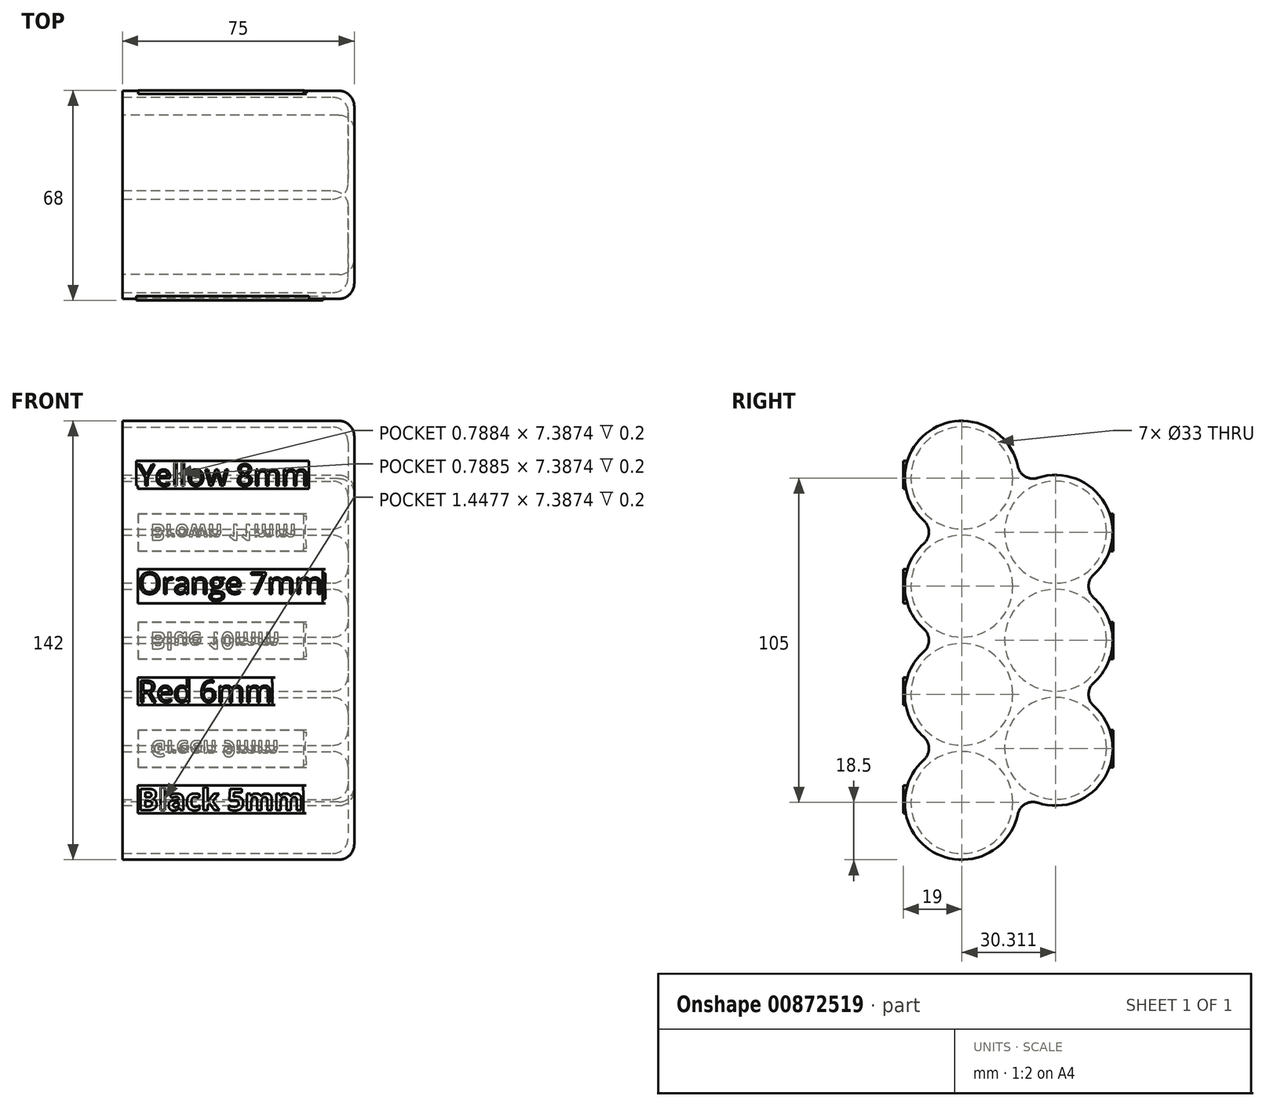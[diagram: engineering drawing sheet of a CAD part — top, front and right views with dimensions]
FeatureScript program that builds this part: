
annotation { "Feature Type Name" : "Feature", "Feature Type Description" : "" }
export const myFeature = defineFeature(function(context is Context, id is Id, definition is map)
    precondition{}
    {
        {
            var Q0;
            Q0=qCreatedBy(makeId("Top.planeOp"),FACE);
            var sketch = newSketch(context, id + "F0", { "sketchPlane" : qUnion([Q0])});
            skCircle(sketch, "E0", {"center": v(0, 0) * mm, "radius": 16.5 * mm});
            skCircle(sketch, "E1.1.0.0", {"center": v(35, 0) * mm, "radius": 16.5 * mm});
            skCircle(sketch, "E1.2.0.0", {"center": v(70, 0) * mm, "radius": 16.5 * mm});
            skCircle(sketch, "E1.3.0.0", {"center": v(105, 0) * mm, "radius": 16.5 * mm});
            skLineSegment(sketch, "E1.direction1", {"start": v(0, 0) * mm, "end": v(35, 0) * mm, "construction": true});
            skCircle(sketch, "E2", {"center": v(17.5, 30.31) * mm, "radius": 16.5 * mm});
            skCircle(sketch, "E3.1.0.0", {"center": v(52.5, 30.31) * mm, "radius": 16.5 * mm});
            skCircle(sketch, "E3.2.0.0", {"center": v(87.5, 30.31) * mm, "radius": 16.5 * mm});
            skLineSegment(sketch, "E3.direction1", {"start": v(17.5, 30.31) * mm, "end": v(52.5, 30.31) * mm, "construction": true});
            skCircle(sketch, "E4", {"center": v(0, 0) * mm, "radius": 18.5 * mm});
            skCircle(sketch, "E5.1.0.0", {"center": v(35, 0) * mm, "radius": 18.5 * mm});
            skCircle(sketch, "E5.2.0.0", {"center": v(70, 0) * mm, "radius": 18.5 * mm});
            skCircle(sketch, "E5.3.0.0", {"center": v(105, 0) * mm, "radius": 18.5 * mm});
            skCircle(sketch, "E6", {"center": v(17.5, 30.31) * mm, "radius": 18.5 * mm});
            skCircle(sketch, "E7.1.0.0", {"center": v(52.5, 30.31) * mm, "radius": 18.5 * mm});
            skCircle(sketch, "E7.2.0.0", {"center": v(87.5, 30.31) * mm, "radius": 18.5 * mm});
            skSolve(sketch);
        }
        {
            var Q0;
            {var subQ0=sQuery(id+"F0.wireOp",EDGE,"E7.1.0.0");var subQ1=sQuery(id+"F0.wireOp",EDGE,"E1.2.0.0");var subQ2=makeQuery(id+"F0.imprint","INTERSECT",VERTEX,{"derivedFrom":[subQ1,subQ0]});Q0=makeQuery(id+"F0.imprint","IMPRINT",FACE,{"disambiguationData":[TD([[makeQuery(id+"F0.imprint","IMPRINT",EDGE,{"disambiguationData":[TD([[subQ2,-1.0]])],"derivedFrom":subQ1}),-1.0]])]});}
            var Q1;
            {var subQ0=sQuery(id+"F0.wireOp",EDGE,"E5.1.0.0");var subQ1=sQuery(id+"F0.wireOp",EDGE,"E0");var subQ2=makeQuery(id+"F0.imprint","INTERSECT",VERTEX,{"derivedFrom":[subQ1,subQ0]});Q1=makeQuery(id+"F0.imprint","IMPRINT",FACE,{"disambiguationData":[TD([[makeQuery(id+"F0.imprint","IMPRINT",EDGE,{"disambiguationData":[TD([[subQ2,-1.0]])],"derivedFrom":subQ1}),-1.0]])]});}
            var Q2;
            {var subQ0=sQuery(id+"F0.wireOp",EDGE,"E7.2.0.0");var subQ1=sQuery(id+"F0.wireOp",EDGE,"E7.1.0.0");var subQ2=makeQuery(id+"F0.imprint","INTERSECT",VERTEX,{"disambiguationData":[OD(0.0)],"derivedFrom":[subQ1,subQ0]});Q2=makeQuery(id+"F0.imprint","IMPRINT",FACE,{"disambiguationData":[TD([[makeQuery(id+"F0.imprint","IMPRINT",EDGE,{"disambiguationData":[TD([[subQ2,1.0]])],"derivedFrom":subQ1}),1.0]])]});}
            var Q3;
            {var subQ0=sQuery(id+"F0.wireOp",EDGE,"E7.2.0.0");var subQ1=sQuery(id+"F0.wireOp",EDGE,"E1.2.0.0");var subQ2=makeQuery(id+"F0.imprint","INTERSECT",VERTEX,{"derivedFrom":[subQ1,subQ0]});Q3=makeQuery(id+"F0.imprint","IMPRINT",FACE,{"disambiguationData":[TD([[makeQuery(id+"F0.imprint","IMPRINT",EDGE,{"disambiguationData":[TD([[subQ2,1.0]])],"derivedFrom":subQ1}),-1.0]])]});}
            var Q4;
            {var subQ0=sQuery(id+"F0.wireOp",EDGE,"E7.2.0.0");var subQ1=sQuery(id+"F0.wireOp",EDGE,"E3.1.0.0");var subQ2=makeQuery(id+"F0.imprint","INTERSECT",VERTEX,{"derivedFrom":[subQ1,subQ0]});Q4=makeQuery(id+"F0.imprint","IMPRINT",FACE,{"disambiguationData":[TD([[makeQuery(id+"F0.imprint","IMPRINT",EDGE,{"disambiguationData":[TD([[subQ2,1.0]])],"derivedFrom":subQ1}),-1.0]])]});}
            var Q5;
            {var subQ0=sQuery(id+"F0.wireOp",EDGE,"E7.1.0.0");var subQ1=sQuery(id+"F0.wireOp",EDGE,"E3.2.0.0");var subQ2=makeQuery(id+"F0.imprint","INTERSECT",VERTEX,{"derivedFrom":[subQ1,subQ0]});Q5=makeQuery(id+"F0.imprint","IMPRINT",FACE,{"disambiguationData":[TD([[makeQuery(id+"F0.imprint","IMPRINT",EDGE,{"disambiguationData":[TD([[subQ2,1.0]])],"derivedFrom":subQ1}),-1.0]])]});}
            var Q6;
            {var subQ0=sQuery(id+"F0.wireOp",EDGE,"E5.2.0.0");var subQ1=sQuery(id+"F0.wireOp",EDGE,"E1.3.0.0");var subQ2=makeQuery(id+"F0.imprint","INTERSECT",VERTEX,{"derivedFrom":[subQ1,subQ0]});Q6=makeQuery(id+"F0.imprint","IMPRINT",FACE,{"disambiguationData":[TD([[makeQuery(id+"F0.imprint","IMPRINT",EDGE,{"disambiguationData":[TD([[subQ2,-1.0]])],"derivedFrom":subQ1}),-1.0]])]});}
            var Q7;
            {var subQ0=sQuery(id+"F0.wireOp",EDGE,"E5.2.0.0");var subQ1=sQuery(id+"F0.wireOp",EDGE,"E1.3.0.0");var subQ2=makeQuery(id+"F0.imprint","INTERSECT",VERTEX,{"derivedFrom":[subQ1,subQ0]});Q7=makeQuery(id+"F0.imprint","IMPRINT",FACE,{"disambiguationData":[TD([[makeQuery(id+"F0.imprint","IMPRINT",EDGE,{"disambiguationData":[TD([[subQ2,1.0]])],"derivedFrom":subQ1}),-1.0]])]});}
            var Q8;
            {var subQ0=sQuery(id+"F0.wireOp",EDGE,"E5.1.0.0");var subQ1=makeQuery(id+"F0.imprint","INTERSECT",VERTEX,{"derivedFrom":[sQuery(id+"F0.wireOp",EDGE,"E1.2.0.0"),subQ0]});Q8=makeQuery(id+"F0.imprint","IMPRINT",FACE,{"disambiguationData":[TD([[makeQuery(id+"F0.imprint","IMPRINT",EDGE,{"disambiguationData":[TD([[subQ1,-1.0]])],"derivedFrom":subQ0}),1.0]])]});}
            var Q9;
            {var subQ0=sQuery(id+"F0.wireOp",EDGE,"E5.1.0.0");var subQ1=sQuery(id+"F0.wireOp",EDGE,"E4");var subQ2=makeQuery(id+"F0.imprint","INTERSECT",VERTEX,{"disambiguationData":[OD(1.0)],"derivedFrom":[subQ1,subQ0]});Q9=makeQuery(id+"F0.imprint","IMPRINT",FACE,{"disambiguationData":[TD([[makeQuery(id+"F0.imprint","IMPRINT",EDGE,{"disambiguationData":[TD([[subQ2,-1.0]])],"derivedFrom":subQ1}),-1.0]])]});}
            var Q10;
            {var subQ0=sQuery(id+"F0.wireOp",EDGE,"E6");var subQ1=sQuery(id+"F0.wireOp",EDGE,"E1.1.0.0");var subQ2=makeQuery(id+"F0.imprint","INTERSECT",VERTEX,{"derivedFrom":[subQ1,subQ0]});Q10=makeQuery(id+"F0.imprint","IMPRINT",FACE,{"disambiguationData":[TD([[makeQuery(id+"F0.imprint","IMPRINT",EDGE,{"disambiguationData":[TD([[subQ2,-1.0]])],"derivedFrom":subQ1}),-1.0]])]});}
            var Q11;
            {var subQ0=sQuery(id+"F0.wireOp",EDGE,"E4");var subQ1=makeQuery(id+"F0.imprint","INTERSECT",VERTEX,{"derivedFrom":[sQuery(id+"F0.wireOp",EDGE,"E2"),subQ0]});Q11=makeQuery(id+"F0.imprint","IMPRINT",FACE,{"disambiguationData":[TD([[makeQuery(id+"F0.imprint","IMPRINT",EDGE,{"disambiguationData":[TD([[subQ1,1.0]])],"derivedFrom":subQ0}),1.0]])]});}
            var Q12;
            {var subQ0=sQuery(id+"F0.wireOp",EDGE,"E5.3.0.0");var subQ1=sQuery(id+"F0.wireOp",EDGE,"E5.2.0.0");var subQ2=makeQuery(id+"F0.imprint","INTERSECT",VERTEX,{"disambiguationData":[OD(1.0)],"derivedFrom":[subQ1,subQ0]});Q12=makeQuery(id+"F0.imprint","IMPRINT",FACE,{"disambiguationData":[TD([[makeQuery(id+"F0.imprint","IMPRINT",EDGE,{"disambiguationData":[TD([[subQ2,-1.0]])],"derivedFrom":subQ1}),-1.0]])]});}
            var Q13;
            {var subQ0=sQuery(id+"F0.wireOp",EDGE,"E5.2.0.0");var subQ1=sQuery(id+"F0.wireOp",EDGE,"E3.2.0.0");var subQ2=makeQuery(id+"F0.imprint","INTERSECT",VERTEX,{"derivedFrom":[subQ1,subQ0]});Q13=makeQuery(id+"F0.imprint","IMPRINT",FACE,{"disambiguationData":[TD([[makeQuery(id+"F0.imprint","IMPRINT",EDGE,{"disambiguationData":[TD([[subQ2,-1.0]])],"derivedFrom":subQ1}),-1.0]])]});}
            var Q14;
            {var subQ0=sQuery(id+"F0.wireOp",EDGE,"E5.1.0.0");var subQ1=sQuery(id+"F0.wireOp",EDGE,"E3.1.0.0");var subQ2=makeQuery(id+"F0.imprint","INTERSECT",VERTEX,{"derivedFrom":[subQ1,subQ0]});Q14=makeQuery(id+"F0.imprint","IMPRINT",FACE,{"disambiguationData":[TD([[makeQuery(id+"F0.imprint","IMPRINT",EDGE,{"disambiguationData":[TD([[subQ2,-1.0]])],"derivedFrom":subQ1}),-1.0]])]});}
            var Q15;
            {var subQ0=sQuery(id+"F0.wireOp",EDGE,"E5.1.0.0");var subQ1=makeQuery(id+"F0.imprint","INTERSECT",VERTEX,{"derivedFrom":[sQuery(id+"F0.wireOp",EDGE,"E3.1.0.0"),subQ0]});Q15=makeQuery(id+"F0.imprint","IMPRINT",FACE,{"disambiguationData":[TD([[makeQuery(id+"F0.imprint","IMPRINT",EDGE,{"disambiguationData":[TD([[subQ1,1.0]])],"derivedFrom":subQ0}),1.0]])]});}
            var Q16;
            {var subQ0=sQuery(id+"F0.wireOp",EDGE,"E6");var subQ1=sQuery(id+"F0.wireOp",EDGE,"E3.1.0.0");var subQ2=makeQuery(id+"F0.imprint","INTERSECT",VERTEX,{"derivedFrom":[subQ1,subQ0]});Q16=makeQuery(id+"F0.imprint","IMPRINT",FACE,{"disambiguationData":[TD([[makeQuery(id+"F0.imprint","IMPRINT",EDGE,{"disambiguationData":[TD([[subQ2,1.0]])],"derivedFrom":subQ1}),-1.0]])]});}
            var Q17;
            {var subQ0=sQuery(id+"F0.wireOp",EDGE,"E5.2.0.0");var subQ1=sQuery(id+"F0.wireOp",EDGE,"E1.1.0.0");var subQ2=makeQuery(id+"F0.imprint","INTERSECT",VERTEX,{"derivedFrom":[subQ1,subQ0]});Q17=makeQuery(id+"F0.imprint","IMPRINT",FACE,{"disambiguationData":[TD([[makeQuery(id+"F0.imprint","IMPRINT",EDGE,{"disambiguationData":[TD([[subQ2,1.0]])],"derivedFrom":subQ1}),-1.0]])]});}
            var Q18;
            {var subQ0=sQuery(id+"F0.wireOp",EDGE,"E4");var subQ1=sQuery(id+"F0.wireOp",EDGE,"E2");var subQ2=makeQuery(id+"F0.imprint","INTERSECT",VERTEX,{"derivedFrom":[subQ1,subQ0]});Q18=makeQuery(id+"F0.imprint","IMPRINT",FACE,{"disambiguationData":[TD([[makeQuery(id+"F0.imprint","IMPRINT",EDGE,{"disambiguationData":[TD([[subQ2,-1.0]])],"derivedFrom":subQ1}),-1.0]])]});}
            var Q19;
            {var subQ0=sQuery(id+"F0.wireOp",EDGE,"E5.2.0.0");var subQ1=sQuery(id+"F0.wireOp",EDGE,"E5.1.0.0");var subQ2=makeQuery(id+"F0.imprint","INTERSECT",VERTEX,{"disambiguationData":[OD(1.0)],"derivedFrom":[subQ1,subQ0]});Q19=makeQuery(id+"F0.imprint","IMPRINT",FACE,{"disambiguationData":[TD([[makeQuery(id+"F0.imprint","IMPRINT",EDGE,{"disambiguationData":[TD([[subQ2,-1.0]])],"derivedFrom":subQ1}),-1.0]])]});}
            var Q20;
            {var subQ0=sQuery(id+"F0.wireOp",EDGE,"E7.2.0.0");var subQ1=sQuery(id+"F0.wireOp",EDGE,"E1.2.0.0");var subQ2=makeQuery(id+"F0.imprint","INTERSECT",VERTEX,{"derivedFrom":[subQ1,subQ0]});Q20=makeQuery(id+"F0.imprint","IMPRINT",FACE,{"disambiguationData":[TD([[makeQuery(id+"F0.imprint","IMPRINT",EDGE,{"disambiguationData":[TD([[subQ2,-1.0]])],"derivedFrom":subQ1}),-1.0]])]});}
            var Q21;
            {var subQ0=sQuery(id+"F0.wireOp",EDGE,"E7.1.0.0");var subQ1=sQuery(id+"F0.wireOp",EDGE,"E2");var subQ2=makeQuery(id+"F0.imprint","INTERSECT",VERTEX,{"derivedFrom":[subQ1,subQ0]});Q21=makeQuery(id+"F0.imprint","IMPRINT",FACE,{"disambiguationData":[TD([[makeQuery(id+"F0.imprint","IMPRINT",EDGE,{"disambiguationData":[TD([[subQ2,1.0]])],"derivedFrom":subQ1}),-1.0]])]});}
            var Q22;
            {var subQ0=sQuery(id+"F0.wireOp",EDGE,"E5.1.0.0");var subQ1=makeQuery(id+"F0.imprint","INTERSECT",VERTEX,{"derivedFrom":[sQuery(id+"F0.wireOp",EDGE,"E2"),subQ0]});Q22=makeQuery(id+"F0.imprint","IMPRINT",FACE,{"disambiguationData":[TD([[makeQuery(id+"F0.imprint","IMPRINT",EDGE,{"disambiguationData":[TD([[subQ1,1.0]])],"derivedFrom":subQ0}),1.0]])]});}
            var Q23;
            {var subQ0=sQuery(id+"F0.wireOp",EDGE,"E6");var subQ1=sQuery(id+"F0.wireOp",EDGE,"E3.1.0.0");var subQ2=makeQuery(id+"F0.imprint","INTERSECT",VERTEX,{"derivedFrom":[subQ1,subQ0]});Q23=makeQuery(id+"F0.imprint","IMPRINT",FACE,{"disambiguationData":[TD([[makeQuery(id+"F0.imprint","IMPRINT",EDGE,{"disambiguationData":[TD([[subQ2,-1.0]])],"derivedFrom":subQ1}),-1.0]])]});}
            var Q24;
            {var subQ0=sQuery(id+"F0.wireOp",EDGE,"E4");var subQ1=makeQuery(id+"F0.imprint","INTERSECT",VERTEX,{"derivedFrom":[sQuery(id+"F0.wireOp",EDGE,"E1.1.0.0"),subQ0]});Q24=makeQuery(id+"F0.imprint","IMPRINT",FACE,{"disambiguationData":[TD([[makeQuery(id+"F0.imprint","IMPRINT",EDGE,{"disambiguationData":[TD([[subQ1,-1.0]])],"derivedFrom":subQ0}),1.0]])]});}
            var Q25;
            {var subQ0=sQuery(id+"F0.wireOp",EDGE,"E4");var subQ1=sQuery(id+"F0.wireOp",EDGE,"E2");var subQ2=makeQuery(id+"F0.imprint","INTERSECT",VERTEX,{"derivedFrom":[subQ1,subQ0]});Q25=makeQuery(id+"F0.imprint","IMPRINT",FACE,{"disambiguationData":[TD([[makeQuery(id+"F0.imprint","IMPRINT",EDGE,{"disambiguationData":[TD([[subQ2,1.0]])],"derivedFrom":subQ1}),-1.0]])]});}
            var Q26;
            {var subQ0=sQuery(id+"F0.wireOp",EDGE,"E5.2.0.0");var subQ1=makeQuery(id+"F0.imprint","INTERSECT",VERTEX,{"derivedFrom":[sQuery(id+"F0.wireOp",EDGE,"E3.2.0.0"),subQ0]});Q26=makeQuery(id+"F0.imprint","IMPRINT",FACE,{"disambiguationData":[TD([[makeQuery(id+"F0.imprint","IMPRINT",EDGE,{"disambiguationData":[TD([[subQ1,1.0]])],"derivedFrom":subQ0}),1.0]])]});}
            var Q27;
            {var subQ0=sQuery(id+"F0.wireOp",EDGE,"E7.1.0.0");var subQ1=sQuery(id+"F0.wireOp",EDGE,"E5.1.0.0");var subQ2=makeQuery(id+"F0.imprint","INTERSECT",VERTEX,{"disambiguationData":[OD(1.0)],"derivedFrom":[subQ1,subQ0]});Q27=makeQuery(id+"F0.imprint","IMPRINT",FACE,{"disambiguationData":[TD([[makeQuery(id+"F0.imprint","IMPRINT",EDGE,{"disambiguationData":[TD([[subQ2,-1.0]])],"derivedFrom":subQ1}),-1.0]])]});}
            var Q28;
            {var subQ0=sQuery(id+"F0.wireOp",EDGE,"E5.2.0.0");var subQ1=sQuery(id+"F0.wireOp",EDGE,"E3.2.0.0");var subQ2=makeQuery(id+"F0.imprint","INTERSECT",VERTEX,{"derivedFrom":[subQ1,subQ0]});Q28=makeQuery(id+"F0.imprint","IMPRINT",FACE,{"disambiguationData":[TD([[makeQuery(id+"F0.imprint","IMPRINT",EDGE,{"disambiguationData":[TD([[subQ2,1.0]])],"derivedFrom":subQ1}),-1.0]])]});}
            var Q29;
            {var subQ0=sQuery(id+"F0.wireOp",EDGE,"E5.3.0.0");var subQ1=sQuery(id+"F0.wireOp",EDGE,"E1.2.0.0");var subQ2=makeQuery(id+"F0.imprint","INTERSECT",VERTEX,{"derivedFrom":[subQ1,subQ0]});Q29=makeQuery(id+"F0.imprint","IMPRINT",FACE,{"disambiguationData":[TD([[makeQuery(id+"F0.imprint","IMPRINT",EDGE,{"disambiguationData":[TD([[subQ2,1.0]])],"derivedFrom":subQ1}),-1.0]])]});}
            var Q30;
            {var subQ0=sQuery(id+"F0.wireOp",EDGE,"E7.1.0.0");var subQ1=sQuery(id+"F0.wireOp",EDGE,"E1.1.0.0");var subQ2=makeQuery(id+"F0.imprint","INTERSECT",VERTEX,{"derivedFrom":[subQ1,subQ0]});Q30=makeQuery(id+"F0.imprint","IMPRINT",FACE,{"disambiguationData":[TD([[makeQuery(id+"F0.imprint","IMPRINT",EDGE,{"disambiguationData":[TD([[subQ2,-1.0]])],"derivedFrom":subQ1}),-1.0]])]});}
            var Q31;
            {var subQ0=sQuery(id+"F0.wireOp",EDGE,"E5.2.0.0");var subQ1=makeQuery(id+"F0.imprint","INTERSECT",VERTEX,{"derivedFrom":[sQuery(id+"F0.wireOp",EDGE,"E1.3.0.0"),subQ0]});Q31=makeQuery(id+"F0.imprint","IMPRINT",FACE,{"disambiguationData":[TD([[makeQuery(id+"F0.imprint","IMPRINT",EDGE,{"disambiguationData":[TD([[subQ1,-1.0]])],"derivedFrom":subQ0}),1.0]])]});}
            var Q32;
            {var subQ0=sQuery(id+"F0.wireOp",EDGE,"E7.2.0.0");var subQ1=sQuery(id+"F0.wireOp",EDGE,"E5.2.0.0");var subQ2=makeQuery(id+"F0.imprint","INTERSECT",VERTEX,{"disambiguationData":[OD(1.0)],"derivedFrom":[subQ1,subQ0]});Q32=makeQuery(id+"F0.imprint","IMPRINT",FACE,{"disambiguationData":[TD([[makeQuery(id+"F0.imprint","IMPRINT",EDGE,{"disambiguationData":[TD([[subQ2,-1.0]])],"derivedFrom":subQ1}),-1.0]])]});}
            var Q33;
            {var subQ0=sQuery(id+"F0.wireOp",EDGE,"E7.1.0.0");var subQ1=sQuery(id+"F0.wireOp",EDGE,"E1.1.0.0");var subQ2=makeQuery(id+"F0.imprint","INTERSECT",VERTEX,{"derivedFrom":[subQ1,subQ0]});Q33=makeQuery(id+"F0.imprint","IMPRINT",FACE,{"disambiguationData":[TD([[makeQuery(id+"F0.imprint","IMPRINT",EDGE,{"disambiguationData":[TD([[subQ2,1.0]])],"derivedFrom":subQ1}),-1.0]])]});}
            var Q34;
            {var subQ0=sQuery(id+"F0.wireOp",EDGE,"E5.2.0.0");var subQ1=makeQuery(id+"F0.imprint","INTERSECT",VERTEX,{"derivedFrom":[sQuery(id+"F0.wireOp",EDGE,"E3.1.0.0"),subQ0]});Q34=makeQuery(id+"F0.imprint","IMPRINT",FACE,{"disambiguationData":[TD([[makeQuery(id+"F0.imprint","IMPRINT",EDGE,{"disambiguationData":[TD([[subQ1,1.0]])],"derivedFrom":subQ0}),1.0]])]});}
            var Q35;
            {var subQ0=sQuery(id+"F0.wireOp",EDGE,"E7.2.0.0");var subQ1=sQuery(id+"F0.wireOp",EDGE,"E5.3.0.0");var subQ2=makeQuery(id+"F0.imprint","INTERSECT",VERTEX,{"disambiguationData":[OD(0.0)],"derivedFrom":[subQ1,subQ0]});Q35=makeQuery(id+"F0.imprint","IMPRINT",FACE,{"disambiguationData":[TD([[makeQuery(id+"F0.imprint","IMPRINT",EDGE,{"disambiguationData":[TD([[subQ2,-1.0]])],"derivedFrom":subQ1}),1.0]])]});}
            var Q36;
            {var subQ0=sQuery(id+"F0.wireOp",EDGE,"E5.1.0.0");var subQ1=sQuery(id+"F0.wireOp",EDGE,"E0");var subQ2=makeQuery(id+"F0.imprint","INTERSECT",VERTEX,{"derivedFrom":[subQ1,subQ0]});Q36=makeQuery(id+"F0.imprint","IMPRINT",FACE,{"disambiguationData":[TD([[makeQuery(id+"F0.imprint","IMPRINT",EDGE,{"disambiguationData":[TD([[subQ2,1.0]])],"derivedFrom":subQ1}),-1.0]])]});}
            var Q37;
            {var subQ0=sQuery(id+"F0.wireOp",EDGE,"E7.1.0.0");var subQ1=sQuery(id+"F0.wireOp",EDGE,"E6");var subQ2=makeQuery(id+"F0.imprint","INTERSECT",VERTEX,{"disambiguationData":[OD(0.0)],"derivedFrom":[subQ1,subQ0]});Q37=makeQuery(id+"F0.imprint","IMPRINT",FACE,{"disambiguationData":[TD([[makeQuery(id+"F0.imprint","IMPRINT",EDGE,{"disambiguationData":[TD([[subQ2,1.0]])],"derivedFrom":subQ1}),1.0]])]});}
            extrude(context, id + "F1", {"entities" : qUnion([Q0, Q1, Q2, Q3, Q4, Q5, Q6, Q7, Q8, Q9, Q10, Q11, Q12, Q13, Q14, Q15, Q16, Q17, Q18, Q19, Q20, Q21, Q22, Q23, Q24, Q25, Q26, Q27, Q28, Q29, Q30, Q31, Q32, Q33, Q34, Q35, Q36, Q37]), "depth" : 75 * mm, "offsetDistance" : 25 * mm});
        }
        {
            var Q0;
            {var subQ0=sQuery(id+"F0.wireOp",EDGE,"E0");var subQ1=makeQuery(id+"F0.imprint","INTERSECT",VERTEX,{"derivedFrom":[subQ0,sQuery(id+"F0.wireOp",EDGE,"E5.1.0.0")]});Q0=makeQuery(id+"F0.imprint","IMPRINT",FACE,{"disambiguationData":[TD([[makeQuery(id+"F0.imprint","IMPRINT",EDGE,{"disambiguationData":[TD([[subQ1,-1.0]])],"derivedFrom":subQ0}),1.0]])]});}
            var Q1;
            {var subQ0=sQuery(id+"F0.wireOp",EDGE,"E2");var subQ1=makeQuery(id+"F0.imprint","INTERSECT",VERTEX,{"derivedFrom":[subQ0,sQuery(id+"F0.wireOp",EDGE,"E4")]});Q1=makeQuery(id+"F0.imprint","IMPRINT",FACE,{"disambiguationData":[TD([[makeQuery(id+"F0.imprint","IMPRINT",EDGE,{"disambiguationData":[TD([[subQ1,1.0]])],"derivedFrom":subQ0}),1.0]])]});}
            var Q2;
            {var subQ0=sQuery(id+"F0.wireOp",EDGE,"E3.1.0.0");var subQ1=makeQuery(id+"F0.imprint","INTERSECT",VERTEX,{"derivedFrom":[subQ0,sQuery(id+"F0.wireOp",EDGE,"E6")]});Q2=makeQuery(id+"F0.imprint","IMPRINT",FACE,{"disambiguationData":[TD([[makeQuery(id+"F0.imprint","IMPRINT",EDGE,{"disambiguationData":[TD([[subQ1,1.0]])],"derivedFrom":subQ0}),1.0]])]});}
            var Q3;
            {var subQ0=sQuery(id+"F0.wireOp",EDGE,"E3.2.0.0");var subQ1=makeQuery(id+"F0.imprint","INTERSECT",VERTEX,{"derivedFrom":[subQ0,sQuery(id+"F0.wireOp",EDGE,"E5.2.0.0")]});Q3=makeQuery(id+"F0.imprint","IMPRINT",FACE,{"disambiguationData":[TD([[makeQuery(id+"F0.imprint","IMPRINT",EDGE,{"disambiguationData":[TD([[subQ1,1.0]])],"derivedFrom":subQ0}),1.0]])]});}
            var Q4;
            {var subQ0=sQuery(id+"F0.wireOp",EDGE,"E1.3.0.0");var subQ1=makeQuery(id+"F0.imprint","INTERSECT",VERTEX,{"derivedFrom":[subQ0,sQuery(id+"F0.wireOp",EDGE,"E5.2.0.0")]});Q4=makeQuery(id+"F0.imprint","IMPRINT",FACE,{"disambiguationData":[TD([[makeQuery(id+"F0.imprint","IMPRINT",EDGE,{"disambiguationData":[TD([[subQ1,1.0]])],"derivedFrom":subQ0}),1.0]])]});}
            var Q5;
            {var subQ0=sQuery(id+"F0.wireOp",EDGE,"E1.2.0.0");var subQ1=makeQuery(id+"F0.imprint","INTERSECT",VERTEX,{"derivedFrom":[subQ0,sQuery(id+"F0.wireOp",EDGE,"E7.2.0.0")]});Q5=makeQuery(id+"F0.imprint","IMPRINT",FACE,{"disambiguationData":[TD([[makeQuery(id+"F0.imprint","IMPRINT",EDGE,{"disambiguationData":[TD([[subQ1,1.0]])],"derivedFrom":subQ0}),1.0]])]});}
            var Q6;
            {var subQ0=sQuery(id+"F0.wireOp",EDGE,"E1.1.0.0");var subQ1=makeQuery(id+"F0.imprint","INTERSECT",VERTEX,{"derivedFrom":[subQ0,sQuery(id+"F0.wireOp",EDGE,"E7.1.0.0")]});Q6=makeQuery(id+"F0.imprint","IMPRINT",FACE,{"disambiguationData":[TD([[makeQuery(id+"F0.imprint","IMPRINT",EDGE,{"disambiguationData":[TD([[subQ1,1.0]])],"derivedFrom":subQ0}),1.0]])]});}
            extrude(context, id + "F2", {"entities" : qUnion([Q0, Q1, Q2, Q3, Q4, Q5, Q6]), "operationType" : NewBodyOperationType.ADD, "depth" : 2 * mm, "offsetDistance" : 25 * mm});
        }
        {
            var Q0;
            Q0=makeQuery(id+"F1.opExtrude","SWEPT_EDGE",EDGE,{"disambiguationData":[OSD([sQuery(id+"F0.wireOp",EDGE,"E5.2.0.0"),sQuery(id+"F0.wireOp",EDGE,"E5.3.0.0")])]});
            var Q1;
            Q1=makeQuery(id+"F1.opExtrude","SWEPT_EDGE",EDGE,{"disambiguationData":[OSD([sQuery(id+"F0.wireOp",EDGE,"E5.1.0.0"),sQuery(id+"F0.wireOp",EDGE,"E5.2.0.0")])]});
            var Q2;
            Q2=makeQuery(id+"F1.opExtrude","SWEPT_EDGE",EDGE,{"disambiguationData":[OSD([sQuery(id+"F0.wireOp",EDGE,"E4"),sQuery(id+"F0.wireOp",EDGE,"E5.1.0.0")])]});
            var Q3;
            Q3=makeQuery(id+"F1.opExtrude","SWEPT_EDGE",EDGE,{"disambiguationData":[OSD([sQuery(id+"F0.wireOp",EDGE,"E7.1.0.0"),sQuery(id+"F0.wireOp",EDGE,"E7.2.0.0")])]});
            var Q4;
            Q4=makeQuery(id+"F1.opExtrude","SWEPT_EDGE",EDGE,{"disambiguationData":[OSD([sQuery(id+"F0.wireOp",EDGE,"E6"),sQuery(id+"F0.wireOp",EDGE,"E7.1.0.0")])]});
            var Q5;
            Q5=makeQuery(id+"F1.opExtrude","SWEPT_EDGE",EDGE,{"disambiguationData":[OSD([sQuery(id+"F0.wireOp",EDGE,"E4"),sQuery(id+"F0.wireOp",EDGE,"E6")])]});
            var Q6;
            Q6=makeQuery(id+"F1.opExtrude","SWEPT_EDGE",EDGE,{"disambiguationData":[OSD([sQuery(id+"F0.wireOp",EDGE,"E5.3.0.0"),sQuery(id+"F0.wireOp",EDGE,"E7.2.0.0")])]});
            fillet(context, id + "F3", {"entities" : qUnion([Q0, Q1, Q2, Q3, Q4, Q5, Q6]), "radius" : 5 * mm, "tangentPropagation" : true, "allowEdgeOverflow" : false});
        }
        {
            var Q0;
            {var subQ0=sQuery(id+"F0.wireOp",EDGE,"E3.2.0.0");var subQ1=sQuery(id+"F0.wireOp",EDGE,"E3.1.0.0");var subQ2=sQuery(id+"F0.wireOp",EDGE,"E2");var subQ3=sQuery(id+"F0.wireOp",EDGE,"E1.3.0.0");var subQ4=sQuery(id+"F0.wireOp",EDGE,"E1.2.0.0");var subQ5=sQuery(id+"F0.wireOp",EDGE,"E1.1.0.0");var subQ6=sQuery(id+"F0.wireOp",EDGE,"E0");Q0=makeQuery(id+"F2.boolean.opBoolean","MERGE",FACE,{"derivedFrom":[makeQuery(id+"F1.opExtrude","CAP_FACE",FACE,{"disambiguationData":[OSD([subQ6,subQ5,subQ4,subQ3,subQ2,subQ1,subQ0,sQuery(id+"F0.wireOp",EDGE,"E4"),sQuery(id+"F0.wireOp",EDGE,"E5.1.0.0"),sQuery(id+"F0.wireOp",EDGE,"E5.2.0.0"),sQuery(id+"F0.wireOp",EDGE,"E5.3.0.0"),sQuery(id+"F0.wireOp",EDGE,"E6"),sQuery(id+"F0.wireOp",EDGE,"E7.1.0.0"),sQuery(id+"F0.wireOp",EDGE,"E7.2.0.0")])],"isStart":true}),makeQuery(id+"F2.opExtrude","CAP_FACE",FACE,{"disambiguationData":[OSD([subQ6])],"isStart":true}),makeQuery(id+"F2.opExtrude","CAP_FACE",FACE,{"disambiguationData":[OSD([subQ5])],"isStart":true}),makeQuery(id+"F2.opExtrude","CAP_FACE",FACE,{"disambiguationData":[OSD([subQ4])],"isStart":true}),makeQuery(id+"F2.opExtrude","CAP_FACE",FACE,{"disambiguationData":[OSD([subQ3])],"isStart":true}),makeQuery(id+"F2.opExtrude","CAP_FACE",FACE,{"disambiguationData":[OSD([subQ2])],"isStart":true}),makeQuery(id+"F2.opExtrude","CAP_FACE",FACE,{"disambiguationData":[OSD([subQ1])],"isStart":true}),makeQuery(id+"F2.opExtrude","CAP_FACE",FACE,{"disambiguationData":[OSD([subQ0])],"isStart":true})]});}
            fillet(context, id + "F4", {"entities" : qUnion([Q0]), "radius" : 5 * mm, "tangentPropagation" : true, "allowEdgeOverflow" : false});
        }
        {
            var Q0;
            Q0=makeQuery(id+"F2.opExtrude","CAP_FACE",FACE,{"disambiguationData":[OSD([sQuery(id+"F0.wireOp",EDGE,"E2")])],"isStart":false});
            var Q1;
            Q1=makeQuery(id+"F2.opExtrude","CAP_FACE",FACE,{"disambiguationData":[OSD([sQuery(id+"F0.wireOp",EDGE,"E3.1.0.0")])],"isStart":false});
            var Q2;
            Q2=makeQuery(id+"F2.opExtrude","CAP_FACE",FACE,{"disambiguationData":[OSD([sQuery(id+"F0.wireOp",EDGE,"E3.2.0.0")])],"isStart":false});
            var Q3;
            Q3=makeQuery(id+"F2.opExtrude","CAP_FACE",FACE,{"disambiguationData":[OSD([sQuery(id+"F0.wireOp",EDGE,"E1.3.0.0")])],"isStart":false});
            var Q4;
            Q4=makeQuery(id+"F2.opExtrude","CAP_FACE",FACE,{"disambiguationData":[OSD([sQuery(id+"F0.wireOp",EDGE,"E1.2.0.0")])],"isStart":false});
            var Q5;
            Q5=makeQuery(id+"F2.opExtrude","CAP_FACE",FACE,{"disambiguationData":[OSD([sQuery(id+"F0.wireOp",EDGE,"E1.1.0.0")])],"isStart":false});
            var Q6;
            Q6=makeQuery(id+"F2.opExtrude","CAP_FACE",FACE,{"disambiguationData":[OSD([sQuery(id+"F0.wireOp",EDGE,"E0")])],"isStart":false});
            fillet(context, id + "F5", {"entities" : qUnion([Q0, Q1, Q2, Q3, Q4, Q5, Q6]), "radius" : 5 * mm, "tangentPropagation" : true, "allowEdgeOverflow" : false});
        }
        {
            var Q0;
            Q0=qCreatedBy(makeId("Front.planeOp"),FACE);
            cPlane(context, id + "F6", {"entities" : qUnion([Q0]), "cplaneType" : CPlaneType.OFFSET, "offset" : 19 * mm, "width" : 150 * mm, "height" : 150 * mm});
        }
        {
            var Q0;
            Q0=qCreatedBy(makeId("Right.planeOp"),FACE);
            var sketch = newSketch(context, id + "F7", { "sketchPlane" : qUnion([Q0])});
            skLineSegment(sketch, "E8", {"start": v(0, 0) * mm, "end": v(-52.63, 0) * mm, "construction": true});
            skSolve(sketch);
        }
        {
            var Q0;
            Q0=makeQuery(id+"F1.opExtrude","SWEPT_BODY",BODY,{"disambiguationData":[OSD([sQuery(id+"F0.wireOp",EDGE,"E0"),sQuery(id+"F0.wireOp",EDGE,"E1.1.0.0"),sQuery(id+"F0.wireOp",EDGE,"E1.2.0.0"),sQuery(id+"F0.wireOp",EDGE,"E1.3.0.0"),sQuery(id+"F0.wireOp",EDGE,"E2"),sQuery(id+"F0.wireOp",EDGE,"E3.1.0.0"),sQuery(id+"F0.wireOp",EDGE,"E3.2.0.0"),sQuery(id+"F0.wireOp",EDGE,"E4"),sQuery(id+"F0.wireOp",EDGE,"E5.1.0.0"),sQuery(id+"F0.wireOp",EDGE,"E5.2.0.0"),sQuery(id+"F0.wireOp",EDGE,"E5.3.0.0"),sQuery(id+"F0.wireOp",EDGE,"E6"),sQuery(id+"F0.wireOp",EDGE,"E7.1.0.0"),sQuery(id+"F0.wireOp",EDGE,"E7.2.0.0")])]});
            var Q1;
            Q1=sQuery(id+"F7.wireOp",EDGE,"E8");
            transform(context, id + "F8", {"entities" : qUnion([Q0]), "transformType" : TransformType.ROTATION, "transformAxis" : qUnion([Q1]), "angle" : 90 * degree, "makeCopy" : false});
        }
        {
            var Q0;
            Q0=qCreatedBy(id+"F6.planeOp",FACE);
            var sketch = newSketch(context, id + "F9", { "sketchPlane" : qUnion([Q0])});
            skLineSegment(sketch, "E9", {"start": v(-70, -17.5) * mm, "end": v(-70, 139.56) * mm, "construction": true});
            skText(sketch, "E10", { "text": "Black 5mm", "fontName": "OpenSans-Bold.ttf"});
            skText(sketch, "E11", { "text": "Red 6mm\n", "fontName": "OpenSans-Regular.ttf"});
            skText(sketch, "E12", { "text": "Orange 7mm\n", "fontName": "OpenSans-Regular.ttf"});
            skText(sketch, "E13", { "text": "Yellow 8mm\n", "fontName": "OpenSans-Regular.ttf"});
            skLineSegment(sketch, "E14.bottom", {"start": v(-70, 5.5) * mm, "end": v(-16.53, 5.5) * mm});
            skLineSegment(sketch, "E14.top", {"start": v(-70, -3.5) * mm, "end": v(-16.53, -3.5) * mm});
            skLineSegment(sketch, "E14.left", {"start": v(-70, 5.5) * mm, "end": v(-70, -3.5) * mm});
            skLineSegment(sketch, "E14.right", {"start": v(-16.53, 5.5) * mm, "end": v(-16.53, -3.5) * mm});
            skLineSegment(sketch, "E15.bottom", {"start": v(-70, 40.5) * mm, "end": v(-26.56, 40.5) * mm});
            skLineSegment(sketch, "E15.top", {"start": v(-70, 31.5) * mm, "end": v(-26.56, 31.5) * mm});
            skLineSegment(sketch, "E15.left", {"start": v(-70, 40.5) * mm, "end": v(-70, 31.5) * mm});
            skLineSegment(sketch, "E15.right", {"start": v(-26.56, 40.5) * mm, "end": v(-26.56, 31.5) * mm});
            skLineSegment(sketch, "E16.bottom", {"start": v(-70, 75.5) * mm, "end": v(-10.3, 75.5) * mm});
            skLineSegment(sketch, "E16.top", {"start": v(-70, 64.5) * mm, "end": v(-10.3, 64.5) * mm});
            skLineSegment(sketch, "E16.left", {"start": v(-70, 75.5) * mm, "end": v(-70, 64.5) * mm});
            skLineSegment(sketch, "E16.right", {"start": v(-10.3, 75.5) * mm, "end": v(-10.3, 64.5) * mm});
            skPoint(sketch, "E17.oppositeSnap0", {"position": v(-14.73, 106) * mm});
            skLineSegment(sketch, "E17.bottom", {"start": v(-70, 110.5) * mm, "end": v(-14.73, 110.5) * mm});
            skLineSegment(sketch, "E17.top", {"start": v(-70, 101.5) * mm, "end": v(-14.73, 101.5) * mm});
            skLineSegment(sketch, "E17.left", {"start": v(-70, 110.5) * mm, "end": v(-70, 101.5) * mm});
            skLineSegment(sketch, "E17.right", {"start": v(-14.73, 110.5) * mm, "end": v(-14.73, 101.5) * mm});
            skLineSegment(sketch, "E18.bottom", {"start": v(-70, 110.5) * mm, "end": v(-70.5, 110.5) * mm});
            skLineSegment(sketch, "E18.top", {"start": v(-70, 102.5) * mm, "end": v(-70.5, 102.5) * mm});
            skLineSegment(sketch, "E18.left", {"start": v(-70, 110.5) * mm, "end": v(-70, 102.5) * mm});
            skLineSegment(sketch, "E18.right", {"start": v(-70.5, 110.5) * mm, "end": v(-70.5, 102.5) * mm});
            skLineSegment(sketch, "E19.bottom", {"start": v(-70.5, 102.5) * mm, "end": v(-70, 102.5) * mm});
            skLineSegment(sketch, "E19.top", {"start": v(-70.5, 101.5) * mm, "end": v(-70, 101.5) * mm});
            skLineSegment(sketch, "E19.left", {"start": v(-70.5, 102.5) * mm, "end": v(-70.5, 101.5) * mm});
            skLineSegment(sketch, "E19.right", {"start": v(-70, 102.5) * mm, "end": v(-70, 101.5) * mm});
            const initialGuessF9  = {"E10": [-0.07, -0.0025, 1, 0, 0.007], "E11": [-0.07, 0.0325, 1, 0, 0.007], "E12": [-0.07, 0.0675, 1, 0, 0.007], "E13": [-0.07, 0.1025, 1, 0, 0.007]};
            skSetInitialGuess(sketch, initialGuessF9);
            skSolve(sketch);
        }
        {
            var Q0;
            Q0=makeQuery(id+"F9.imprint","IMPRINT",FACE,{"disambiguationData":[TD([[makeQuery(id+"F9.imprint","IMPRINT",EDGE,{"derivedFrom":sQuery(id+"F9.wireOp",EDGE,"E10.sketch_text.stroke-0")}),1.0]])]});
            var Q1;
            Q1=makeQuery(id+"F9.imprint","IMPRINT",FACE,{"disambiguationData":[TD([[makeQuery(id+"F9.imprint","IMPRINT",EDGE,{"derivedFrom":sQuery(id+"F9.wireOp",EDGE,"E10.sketch_text.stroke-47")}),1.0]])]});
            var Q2;
            Q2=makeQuery(id+"F9.imprint","IMPRINT",FACE,{"disambiguationData":[TD([[makeQuery(id+"F9.imprint","IMPRINT",EDGE,{"derivedFrom":sQuery(id+"F9.wireOp",EDGE,"E10.sketch_text.stroke-19")}),1.0]])]});
            var Q3;
            Q3=makeQuery(id+"F9.imprint","IMPRINT",FACE,{"disambiguationData":[TD([[makeQuery(id+"F9.imprint","IMPRINT",EDGE,{"derivedFrom":sQuery(id+"F9.wireOp",EDGE,"E10.sketch_text.stroke-12")}),1.0]])]});
            var Q4;
            Q4=makeQuery(id+"F9.imprint","IMPRINT",FACE,{"disambiguationData":[TD([[makeQuery(id+"F9.imprint","IMPRINT",EDGE,{"derivedFrom":sQuery(id+"F9.wireOp",EDGE,"E11.sketch_text.stroke-0")}),1.0]])]});
            var Q5;
            Q5=makeQuery(id+"F9.imprint","IMPRINT",FACE,{"disambiguationData":[TD([[makeQuery(id+"F9.imprint","IMPRINT",EDGE,{"derivedFrom":sQuery(id+"F9.wireOp",EDGE,"E11.sketch_text.stroke-76")}),1.0]])]});
            var Q6;
            Q6=makeQuery(id+"F9.imprint","IMPRINT",FACE,{"disambiguationData":[TD([[makeQuery(id+"F9.imprint","IMPRINT",EDGE,{"derivedFrom":sQuery(id+"F9.wireOp",EDGE,"E11.sketch_text.stroke-52")}),1.0]])]});
            var Q7;
            Q7=makeQuery(id+"F9.imprint","IMPRINT",FACE,{"disambiguationData":[TD([[makeQuery(id+"F9.imprint","IMPRINT",EDGE,{"derivedFrom":sQuery(id+"F9.wireOp",EDGE,"E11.sketch_text.stroke-11")}),1.0]])]});
            var Q8;
            Q8=makeQuery(id+"F9.imprint","IMPRINT",FACE,{"disambiguationData":[TD([[makeQuery(id+"F9.imprint","IMPRINT",EDGE,{"derivedFrom":sQuery(id+"F9.wireOp",EDGE,"E11.sketch_text.stroke-32")}),1.0]])]});
            var Q9;
            Q9=makeQuery(id+"F9.imprint","IMPRINT",FACE,{"disambiguationData":[TD([[makeQuery(id+"F9.imprint","IMPRINT",EDGE,{"derivedFrom":sQuery(id+"F9.wireOp",EDGE,"E12.sketch_text.stroke-0")}),1.0]])]});
            var Q10;
            Q10=makeQuery(id+"F9.imprint","IMPRINT",FACE,{"disambiguationData":[TD([[makeQuery(id+"F9.imprint","IMPRINT",EDGE,{"derivedFrom":sQuery(id+"F9.wireOp",EDGE,"E12.sketch_text.stroke-48")}),1.0]])]});
            var Q11;
            Q11=makeQuery(id+"F9.imprint","IMPRINT",FACE,{"disambiguationData":[TD([[makeQuery(id+"F9.imprint","IMPRINT",EDGE,{"derivedFrom":sQuery(id+"F9.wireOp",EDGE,"E12.sketch_text.stroke-8")}),1.0]])]});
            var Q12;
            Q12=makeQuery(id+"F9.imprint","IMPRINT",FACE,{"disambiguationData":[TD([[makeQuery(id+"F9.imprint","IMPRINT",EDGE,{"derivedFrom":sQuery(id+"F9.wireOp",EDGE,"E12.sketch_text.stroke-111")}),1.0]])]});
            var Q13;
            Q13=makeQuery(id+"F9.imprint","IMPRINT",FACE,{"disambiguationData":[TD([[makeQuery(id+"F9.imprint","IMPRINT",EDGE,{"derivedFrom":sQuery(id+"F9.wireOp",EDGE,"E12.sketch_text.stroke-102")}),1.0]])]});
            var Q14;
            Q14=makeQuery(id+"F9.imprint","IMPRINT",FACE,{"disambiguationData":[TD([[makeQuery(id+"F9.imprint","IMPRINT",EDGE,{"derivedFrom":sQuery(id+"F9.wireOp",EDGE,"E12.sketch_text.stroke-131")}),1.0]])]});
            var Q15;
            Q15=makeQuery(id+"F9.imprint","IMPRINT",FACE,{"disambiguationData":[TD([[makeQuery(id+"F9.imprint","IMPRINT",EDGE,{"derivedFrom":sQuery(id+"F9.wireOp",EDGE,"E13.sketch_text.stroke-0")}),1.0]])]});
            var Q16;
            {var subQ3=sQuery(id+"F9.wireOp",EDGE,"E18.bottom");Q16=makeQuery(id+"F9.imprint","IMPRINT",FACE,{"disambiguationData":[TD([[makeQuery(id+"F9.imprint","IMPRINT",EDGE,{"derivedFrom":subQ3}),1.0]])]});}
            var Q17;
            Q17=makeQuery(id+"F9.imprint","IMPRINT",FACE,{"disambiguationData":[TD([[makeQuery(id+"F9.imprint","IMPRINT",EDGE,{"derivedFrom":sQuery(id+"F9.wireOp",EDGE,"E19.bottom")}),-1.0]])]});
            var Q18;
            Q18=makeQuery(id+"F9.imprint","IMPRINT",FACE,{"disambiguationData":[TD([[makeQuery(id+"F9.imprint","IMPRINT",EDGE,{"derivedFrom":sQuery(id+"F9.wireOp",EDGE,"E13.sketch_text.stroke-23")}),1.0]])]});
            var Q19;
            Q19=makeQuery(id+"F9.imprint","IMPRINT",FACE,{"disambiguationData":[TD([[makeQuery(id+"F9.imprint","IMPRINT",EDGE,{"derivedFrom":sQuery(id+"F9.wireOp",EDGE,"E13.sketch_text.stroke-45")}),1.0]])]});
            var Q20;
            Q20=makeQuery(id+"F9.imprint","IMPRINT",FACE,{"disambiguationData":[TD([[makeQuery(id+"F9.imprint","IMPRINT",EDGE,{"derivedFrom":sQuery(id+"F9.wireOp",EDGE,"E13.sketch_text.stroke-91")}),1.0]])]});
            var Q21;
            Q21=makeQuery(id+"F9.imprint","IMPRINT",FACE,{"disambiguationData":[TD([[makeQuery(id+"F9.imprint","IMPRINT",EDGE,{"derivedFrom":sQuery(id+"F9.wireOp",EDGE,"E13.sketch_text.stroke-99")}),1.0]])]});
            var Q22;
            Q22=makeQuery(id+"F9.imprint","IMPRINT",FACE,{"disambiguationData":[TD([[makeQuery(id+"F9.imprint","IMPRINT",EDGE,{"derivedFrom":sQuery(id+"F9.wireOp",EDGE,"E13.sketch_text.stroke-0")}),-1.0]])]});
            var Q23;
            Q23=makeQuery(id+"F9.imprint","IMPRINT",FACE,{"disambiguationData":[TD([[makeQuery(id+"F9.imprint","IMPRINT",EDGE,{"derivedFrom":sQuery(id+"F9.wireOp",EDGE,"E13.sketch_text.stroke-9")}),-1.0]])]});
            var Q24;
            Q24=makeQuery(id+"F9.imprint","IMPRINT",FACE,{"disambiguationData":[TD([[makeQuery(id+"F9.imprint","IMPRINT",EDGE,{"derivedFrom":sQuery(id+"F9.wireOp",EDGE,"E13.sketch_text.stroke-28")}),-1.0]])]});
            var Q25;
            Q25=makeQuery(id+"F9.imprint","IMPRINT",FACE,{"disambiguationData":[TD([[makeQuery(id+"F9.imprint","IMPRINT",EDGE,{"derivedFrom":sQuery(id+"F9.wireOp",EDGE,"E13.sketch_text.stroke-32")}),-1.0]])]});
            var Q26;
            Q26=makeQuery(id+"F9.imprint","IMPRINT",FACE,{"disambiguationData":[TD([[makeQuery(id+"F9.imprint","IMPRINT",EDGE,{"derivedFrom":sQuery(id+"F9.wireOp",EDGE,"E13.sketch_text.stroke-36")}),-1.0]])]});
            var Q27;
            Q27=makeQuery(id+"F9.imprint","IMPRINT",FACE,{"disambiguationData":[TD([[makeQuery(id+"F9.imprint","IMPRINT",EDGE,{"derivedFrom":sQuery(id+"F9.wireOp",EDGE,"E13.sketch_text.stroke-53")}),-1.0]])]});
            var Q28;
            Q28=makeQuery(id+"F9.imprint","IMPRINT",FACE,{"disambiguationData":[TD([[makeQuery(id+"F9.imprint","IMPRINT",EDGE,{"derivedFrom":sQuery(id+"F9.wireOp",EDGE,"E13.sketch_text.stroke-76")}),-1.0]])]});
            var Q29;
            Q29=makeQuery(id+"F9.imprint","IMPRINT",FACE,{"disambiguationData":[TD([[makeQuery(id+"F9.imprint","IMPRINT",EDGE,{"derivedFrom":sQuery(id+"F9.wireOp",EDGE,"E13.sketch_text.stroke-107")}),-1.0]])]});
            var Q30;
            Q30=makeQuery(id+"F9.imprint","IMPRINT",FACE,{"disambiguationData":[TD([[makeQuery(id+"F9.imprint","IMPRINT",EDGE,{"derivedFrom":sQuery(id+"F9.wireOp",EDGE,"E13.sketch_text.stroke-135")}),-1.0]])]});
            var Q31;
            Q31=makeQuery(id+"F9.imprint","IMPRINT",FACE,{"disambiguationData":[TD([[makeQuery(id+"F9.imprint","IMPRINT",EDGE,{"derivedFrom":sQuery(id+"F9.wireOp",EDGE,"E12.sketch_text.stroke-0")}),-1.0]])]});
            var Q32;
            Q32=makeQuery(id+"F9.imprint","IMPRINT",FACE,{"disambiguationData":[TD([[makeQuery(id+"F9.imprint","IMPRINT",EDGE,{"derivedFrom":sQuery(id+"F9.wireOp",EDGE,"E12.sketch_text.stroke-16")}),-1.0]])]});
            var Q33;
            Q33=makeQuery(id+"F9.imprint","IMPRINT",FACE,{"disambiguationData":[TD([[makeQuery(id+"F9.imprint","IMPRINT",EDGE,{"derivedFrom":sQuery(id+"F9.wireOp",EDGE,"E12.sketch_text.stroke-29")}),-1.0]])]});
            var Q34;
            Q34=makeQuery(id+"F9.imprint","IMPRINT",FACE,{"disambiguationData":[TD([[makeQuery(id+"F9.imprint","IMPRINT",EDGE,{"derivedFrom":sQuery(id+"F9.wireOp",EDGE,"E12.sketch_text.stroke-56")}),-1.0]])]});
            var Q35;
            Q35=makeQuery(id+"F9.imprint","IMPRINT",FACE,{"disambiguationData":[TD([[makeQuery(id+"F9.imprint","IMPRINT",EDGE,{"derivedFrom":sQuery(id+"F9.wireOp",EDGE,"E12.sketch_text.stroke-73")}),-1.0]])]});
            var Q36;
            Q36=makeQuery(id+"F9.imprint","IMPRINT",FACE,{"disambiguationData":[TD([[makeQuery(id+"F9.imprint","IMPRINT",EDGE,{"derivedFrom":sQuery(id+"F9.wireOp",EDGE,"E12.sketch_text.stroke-117")}),-1.0]])]});
            var Q37;
            Q37=makeQuery(id+"F9.imprint","IMPRINT",FACE,{"disambiguationData":[TD([[makeQuery(id+"F9.imprint","IMPRINT",EDGE,{"derivedFrom":sQuery(id+"F9.wireOp",EDGE,"E12.sketch_text.stroke-136")}),-1.0]])]});
            var Q38;
            Q38=makeQuery(id+"F9.imprint","IMPRINT",FACE,{"disambiguationData":[TD([[makeQuery(id+"F9.imprint","IMPRINT",EDGE,{"derivedFrom":sQuery(id+"F9.wireOp",EDGE,"E12.sketch_text.stroke-143")}),-1.0]])]});
            var Q39;
            Q39=makeQuery(id+"F9.imprint","IMPRINT",FACE,{"disambiguationData":[TD([[makeQuery(id+"F9.imprint","IMPRINT",EDGE,{"derivedFrom":sQuery(id+"F9.wireOp",EDGE,"E12.sketch_text.stroke-171")}),-1.0]])]});
            var Q40;
            Q40=makeQuery(id+"F9.imprint","IMPRINT",FACE,{"disambiguationData":[TD([[makeQuery(id+"F9.imprint","IMPRINT",EDGE,{"derivedFrom":sQuery(id+"F9.wireOp",EDGE,"E11.sketch_text.stroke-0")}),-1.0]])]});
            var Q41;
            Q41=makeQuery(id+"F9.imprint","IMPRINT",FACE,{"disambiguationData":[TD([[makeQuery(id+"F9.imprint","IMPRINT",EDGE,{"derivedFrom":sQuery(id+"F9.wireOp",EDGE,"E11.sketch_text.stroke-18")}),-1.0]])]});
            var Q42;
            Q42=makeQuery(id+"F9.imprint","IMPRINT",FACE,{"disambiguationData":[TD([[makeQuery(id+"F9.imprint","IMPRINT",EDGE,{"derivedFrom":sQuery(id+"F9.wireOp",EDGE,"E11.sketch_text.stroke-37")}),-1.0]])]});
            var Q43;
            Q43=makeQuery(id+"F9.imprint","IMPRINT",FACE,{"disambiguationData":[TD([[makeQuery(id+"F9.imprint","IMPRINT",EDGE,{"derivedFrom":sQuery(id+"F9.wireOp",EDGE,"E11.sketch_text.stroke-61")}),-1.0]])]});
            var Q44;
            Q44=makeQuery(id+"F9.imprint","IMPRINT",FACE,{"disambiguationData":[TD([[makeQuery(id+"F9.imprint","IMPRINT",EDGE,{"derivedFrom":sQuery(id+"F9.wireOp",EDGE,"E11.sketch_text.stroke-86")}),-1.0]])]});
            var Q45;
            Q45=makeQuery(id+"F9.imprint","IMPRINT",FACE,{"disambiguationData":[TD([[makeQuery(id+"F9.imprint","IMPRINT",EDGE,{"derivedFrom":sQuery(id+"F9.wireOp",EDGE,"E11.sketch_text.stroke-114")}),-1.0]])]});
            var Q46;
            Q46=makeQuery(id+"F9.imprint","IMPRINT",FACE,{"disambiguationData":[TD([[makeQuery(id+"F9.imprint","IMPRINT",EDGE,{"derivedFrom":sQuery(id+"F9.wireOp",EDGE,"E10.sketch_text.stroke-0")}),-1.0]])]});
            var Q47;
            Q47=makeQuery(id+"F9.imprint","IMPRINT",FACE,{"disambiguationData":[TD([[makeQuery(id+"F9.imprint","IMPRINT",EDGE,{"derivedFrom":sQuery(id+"F9.wireOp",EDGE,"E10.sketch_text.stroke-25")}),-1.0]])]});
            var Q48;
            Q48=makeQuery(id+"F9.imprint","IMPRINT",FACE,{"disambiguationData":[TD([[makeQuery(id+"F9.imprint","IMPRINT",EDGE,{"derivedFrom":sQuery(id+"F9.wireOp",EDGE,"E10.sketch_text.stroke-29")}),-1.0]])]});
            var Q49;
            Q49=makeQuery(id+"F9.imprint","IMPRINT",FACE,{"disambiguationData":[TD([[makeQuery(id+"F9.imprint","IMPRINT",EDGE,{"derivedFrom":sQuery(id+"F9.wireOp",EDGE,"E10.sketch_text.stroke-54")}),-1.0]])]});
            var Q50;
            Q50=makeQuery(id+"F9.imprint","IMPRINT",FACE,{"disambiguationData":[TD([[makeQuery(id+"F9.imprint","IMPRINT",EDGE,{"derivedFrom":sQuery(id+"F9.wireOp",EDGE,"E10.sketch_text.stroke-68")}),-1.0]])]});
            var Q51;
            Q51=makeQuery(id+"F9.imprint","IMPRINT",FACE,{"disambiguationData":[TD([[makeQuery(id+"F9.imprint","IMPRINT",EDGE,{"derivedFrom":sQuery(id+"F9.wireOp",EDGE,"E10.sketch_text.stroke-83")}),-1.0]])]});
            var Q52;
            Q52=makeQuery(id+"F9.imprint","IMPRINT",FACE,{"disambiguationData":[TD([[makeQuery(id+"F9.imprint","IMPRINT",EDGE,{"derivedFrom":sQuery(id+"F9.wireOp",EDGE,"E10.sketch_text.stroke-103")}),-1.0]])]});
            var Q53;
            Q53=makeQuery(id+"F9.imprint","IMPRINT",FACE,{"disambiguationData":[TD([[makeQuery(id+"F9.imprint","IMPRINT",EDGE,{"derivedFrom":sQuery(id+"F9.wireOp",EDGE,"E10.sketch_text.stroke-131")}),-1.0]])]});
            extrude(context, id + "F10", {"entities" : qUnion([Q0, Q1, Q2, Q3, Q4, Q5, Q6, Q7, Q8, Q9, Q10, Q11, Q12, Q13, Q14, Q15, Q16, Q17, Q18, Q19, Q20, Q21, Q22, Q23, Q24, Q25, Q26, Q27, Q28, Q29, Q30, Q31, Q32, Q33, Q34, Q35, Q36, Q37, Q38, Q39, Q40, Q41, Q42, Q43, Q44, Q45, Q46, Q47, Q48, Q49, Q50, Q51, Q52, Q53]), "operationType" : NewBodyOperationType.ADD, "oppositeDirection" : true, "depth" : 1.5 * mm, "offsetDistance" : 25 * mm});
        }
        {
            var Q0;
            Q0=makeQuery(id+"F9.imprint","IMPRINT",FACE,{"disambiguationData":[TD([[makeQuery(id+"F9.imprint","IMPRINT",EDGE,{"derivedFrom":sQuery(id+"F9.wireOp",EDGE,"E10.sketch_text.stroke-29")}),-1.0]])]});
            var Q1;
            Q1=makeQuery(id+"F9.imprint","IMPRINT",FACE,{"disambiguationData":[TD([[makeQuery(id+"F9.imprint","IMPRINT",EDGE,{"derivedFrom":sQuery(id+"F9.wireOp",EDGE,"E10.sketch_text.stroke-54")}),-1.0]])]});
            var Q2;
            Q2=makeQuery(id+"F9.imprint","IMPRINT",FACE,{"disambiguationData":[TD([[makeQuery(id+"F9.imprint","IMPRINT",EDGE,{"derivedFrom":sQuery(id+"F9.wireOp",EDGE,"E10.sketch_text.stroke-25")}),-1.0]])]});
            var Q3;
            Q3=makeQuery(id+"F9.imprint","IMPRINT",FACE,{"disambiguationData":[TD([[makeQuery(id+"F9.imprint","IMPRINT",EDGE,{"derivedFrom":sQuery(id+"F9.wireOp",EDGE,"E10.sketch_text.stroke-0")}),-1.0]])]});
            var Q4;
            Q4=makeQuery(id+"F9.imprint","IMPRINT",FACE,{"disambiguationData":[TD([[makeQuery(id+"F9.imprint","IMPRINT",EDGE,{"derivedFrom":sQuery(id+"F9.wireOp",EDGE,"E10.sketch_text.stroke-68")}),-1.0]])]});
            var Q5;
            Q5=makeQuery(id+"F9.imprint","IMPRINT",FACE,{"disambiguationData":[TD([[makeQuery(id+"F9.imprint","IMPRINT",EDGE,{"derivedFrom":sQuery(id+"F9.wireOp",EDGE,"E10.sketch_text.stroke-83")}),-1.0]])]});
            var Q6;
            Q6=makeQuery(id+"F9.imprint","IMPRINT",FACE,{"disambiguationData":[TD([[makeQuery(id+"F9.imprint","IMPRINT",EDGE,{"derivedFrom":sQuery(id+"F9.wireOp",EDGE,"E10.sketch_text.stroke-103")}),-1.0]])]});
            var Q7;
            Q7=makeQuery(id+"F9.imprint","IMPRINT",FACE,{"disambiguationData":[TD([[makeQuery(id+"F9.imprint","IMPRINT",EDGE,{"derivedFrom":sQuery(id+"F9.wireOp",EDGE,"E10.sketch_text.stroke-131")}),-1.0]])]});
            var Q8;
            Q8=makeQuery(id+"F9.imprint","IMPRINT",FACE,{"disambiguationData":[TD([[makeQuery(id+"F9.imprint","IMPRINT",EDGE,{"derivedFrom":sQuery(id+"F9.wireOp",EDGE,"E11.sketch_text.stroke-0")}),-1.0]])]});
            var Q9;
            Q9=makeQuery(id+"F9.imprint","IMPRINT",FACE,{"disambiguationData":[TD([[makeQuery(id+"F9.imprint","IMPRINT",EDGE,{"derivedFrom":sQuery(id+"F9.wireOp",EDGE,"E11.sketch_text.stroke-18")}),-1.0]])]});
            var Q10;
            Q10=makeQuery(id+"F9.imprint","IMPRINT",FACE,{"disambiguationData":[TD([[makeQuery(id+"F9.imprint","IMPRINT",EDGE,{"derivedFrom":sQuery(id+"F9.wireOp",EDGE,"E11.sketch_text.stroke-37")}),-1.0]])]});
            var Q11;
            Q11=makeQuery(id+"F9.imprint","IMPRINT",FACE,{"disambiguationData":[TD([[makeQuery(id+"F9.imprint","IMPRINT",EDGE,{"derivedFrom":sQuery(id+"F9.wireOp",EDGE,"E11.sketch_text.stroke-61")}),-1.0]])]});
            var Q12;
            Q12=makeQuery(id+"F9.imprint","IMPRINT",FACE,{"disambiguationData":[TD([[makeQuery(id+"F9.imprint","IMPRINT",EDGE,{"derivedFrom":sQuery(id+"F9.wireOp",EDGE,"E11.sketch_text.stroke-86")}),-1.0]])]});
            var Q13;
            Q13=makeQuery(id+"F9.imprint","IMPRINT",FACE,{"disambiguationData":[TD([[makeQuery(id+"F9.imprint","IMPRINT",EDGE,{"derivedFrom":sQuery(id+"F9.wireOp",EDGE,"E11.sketch_text.stroke-114")}),-1.0]])]});
            var Q14;
            Q14=makeQuery(id+"F9.imprint","IMPRINT",FACE,{"disambiguationData":[TD([[makeQuery(id+"F9.imprint","IMPRINT",EDGE,{"derivedFrom":sQuery(id+"F9.wireOp",EDGE,"E12.sketch_text.stroke-0")}),-1.0]])]});
            var Q15;
            Q15=makeQuery(id+"F9.imprint","IMPRINT",FACE,{"disambiguationData":[TD([[makeQuery(id+"F9.imprint","IMPRINT",EDGE,{"derivedFrom":sQuery(id+"F9.wireOp",EDGE,"E12.sketch_text.stroke-16")}),-1.0]])]});
            var Q16;
            Q16=makeQuery(id+"F9.imprint","IMPRINT",FACE,{"disambiguationData":[TD([[makeQuery(id+"F9.imprint","IMPRINT",EDGE,{"derivedFrom":sQuery(id+"F9.wireOp",EDGE,"E12.sketch_text.stroke-29")}),-1.0]])]});
            var Q17;
            Q17=makeQuery(id+"F9.imprint","IMPRINT",FACE,{"disambiguationData":[TD([[makeQuery(id+"F9.imprint","IMPRINT",EDGE,{"derivedFrom":sQuery(id+"F9.wireOp",EDGE,"E12.sketch_text.stroke-56")}),-1.0]])]});
            var Q18;
            Q18=makeQuery(id+"F9.imprint","IMPRINT",FACE,{"disambiguationData":[TD([[makeQuery(id+"F9.imprint","IMPRINT",EDGE,{"derivedFrom":sQuery(id+"F9.wireOp",EDGE,"E12.sketch_text.stroke-73")}),-1.0]])]});
            var Q19;
            Q19=makeQuery(id+"F9.imprint","IMPRINT",FACE,{"disambiguationData":[TD([[makeQuery(id+"F9.imprint","IMPRINT",EDGE,{"derivedFrom":sQuery(id+"F9.wireOp",EDGE,"E12.sketch_text.stroke-117")}),-1.0]])]});
            var Q20;
            Q20=makeQuery(id+"F9.imprint","IMPRINT",FACE,{"disambiguationData":[TD([[makeQuery(id+"F9.imprint","IMPRINT",EDGE,{"derivedFrom":sQuery(id+"F9.wireOp",EDGE,"E12.sketch_text.stroke-136")}),-1.0]])]});
            var Q21;
            Q21=makeQuery(id+"F9.imprint","IMPRINT",FACE,{"disambiguationData":[TD([[makeQuery(id+"F9.imprint","IMPRINT",EDGE,{"derivedFrom":sQuery(id+"F9.wireOp",EDGE,"E12.sketch_text.stroke-143")}),-1.0]])]});
            var Q22;
            Q22=makeQuery(id+"F9.imprint","IMPRINT",FACE,{"disambiguationData":[TD([[makeQuery(id+"F9.imprint","IMPRINT",EDGE,{"derivedFrom":sQuery(id+"F9.wireOp",EDGE,"E12.sketch_text.stroke-171")}),-1.0]])]});
            var Q23;
            Q23=makeQuery(id+"F9.imprint","IMPRINT",FACE,{"disambiguationData":[TD([[makeQuery(id+"F9.imprint","IMPRINT",EDGE,{"derivedFrom":sQuery(id+"F9.wireOp",EDGE,"E13.sketch_text.stroke-0")}),-1.0]])]});
            var Q24;
            Q24=makeQuery(id+"F9.imprint","IMPRINT",FACE,{"disambiguationData":[TD([[makeQuery(id+"F9.imprint","IMPRINT",EDGE,{"derivedFrom":sQuery(id+"F9.wireOp",EDGE,"E13.sketch_text.stroke-9")}),-1.0]])]});
            var Q25;
            Q25=makeQuery(id+"F9.imprint","IMPRINT",FACE,{"disambiguationData":[TD([[makeQuery(id+"F9.imprint","IMPRINT",EDGE,{"derivedFrom":sQuery(id+"F9.wireOp",EDGE,"E13.sketch_text.stroke-28")}),-1.0]])]});
            var Q26;
            Q26=makeQuery(id+"F9.imprint","IMPRINT",FACE,{"disambiguationData":[TD([[makeQuery(id+"F9.imprint","IMPRINT",EDGE,{"derivedFrom":sQuery(id+"F9.wireOp",EDGE,"E13.sketch_text.stroke-32")}),-1.0]])]});
            var Q27;
            Q27=makeQuery(id+"F9.imprint","IMPRINT",FACE,{"disambiguationData":[TD([[makeQuery(id+"F9.imprint","IMPRINT",EDGE,{"derivedFrom":sQuery(id+"F9.wireOp",EDGE,"E13.sketch_text.stroke-36")}),-1.0]])]});
            var Q28;
            Q28=makeQuery(id+"F9.imprint","IMPRINT",FACE,{"disambiguationData":[TD([[makeQuery(id+"F9.imprint","IMPRINT",EDGE,{"derivedFrom":sQuery(id+"F9.wireOp",EDGE,"E13.sketch_text.stroke-53")}),-1.0]])]});
            var Q29;
            Q29=makeQuery(id+"F9.imprint","IMPRINT",FACE,{"disambiguationData":[TD([[makeQuery(id+"F9.imprint","IMPRINT",EDGE,{"derivedFrom":sQuery(id+"F9.wireOp",EDGE,"E13.sketch_text.stroke-76")}),-1.0]])]});
            var Q30;
            Q30=makeQuery(id+"F9.imprint","IMPRINT",FACE,{"disambiguationData":[TD([[makeQuery(id+"F9.imprint","IMPRINT",EDGE,{"derivedFrom":sQuery(id+"F9.wireOp",EDGE,"E13.sketch_text.stroke-107")}),-1.0]])]});
            var Q31;
            Q31=makeQuery(id+"F9.imprint","IMPRINT",FACE,{"disambiguationData":[TD([[makeQuery(id+"F9.imprint","IMPRINT",EDGE,{"derivedFrom":sQuery(id+"F9.wireOp",EDGE,"E13.sketch_text.stroke-135")}),-1.0]])]});
            extrude(context, id + "F11", {"entities" : qUnion([Q0, Q1, Q2, Q3, Q4, Q5, Q6, Q7, Q8, Q9, Q10, Q11, Q12, Q13, Q14, Q15, Q16, Q17, Q18, Q19, Q20, Q21, Q22, Q23, Q24, Q25, Q26, Q27, Q28, Q29, Q30, Q31]), "operationType" : NewBodyOperationType.REMOVE, "oppositeDirection" : true, "depth" : .2 * mm, "offsetDistance" : 25 * mm});
        }
        {
            var Q0;
            Q0=qCreatedBy(makeId("Front.planeOp"),FACE);
            cPlane(context, id + "F12", {"entities" : qUnion([Q0]), "cplaneType" : CPlaneType.OFFSET, "offset" : 49 * mm, "oppositeDirection" : true, "width" : 150 * mm, "height" : 150 * mm});
        }
        {
            var Q0;
            Q0=qCreatedBy(id+"F12.planeOp",FACE);
            var sketch = newSketch(context, id + "F13", { "sketchPlane" : qUnion([Q0])});
            skLineSegment(sketch, "E20.0", {"start": v(-75, 71) * mm, "end": v(-75, 104) * mm, "construction": true});
            skLineSegment(sketch, "E21.0", {"start": v(-75, 36) * mm, "end": v(-75, 69) * mm, "construction": true});
            skLineSegment(sketch, "E22.0", {"start": v(-75, 1) * mm, "end": v(-75, 34) * mm, "construction": true});
            skLineSegment(sketch, "E23.0", {"start": v(-70, -17.5) * mm, "end": v(-70, 139.56) * mm, "construction": true});
            skLineSegment(sketch, "E24.bottom", {"start": v(-70, 11.5) * mm, "end": v(-16.47, 11.5) * mm});
            skLineSegment(sketch, "E24.top", {"start": v(-70, 23.5) * mm, "end": v(-16.47, 23.5) * mm});
            skLineSegment(sketch, "E24.left", {"start": v(-70, 11.5) * mm, "end": v(-70, 23.5) * mm});
            skLineSegment(sketch, "E24.right", {"start": v(-16.47, 11.5) * mm, "end": v(-16.47, 23.5) * mm});
            skLineSegment(sketch, "E25.bottom", {"start": v(-70, 46.5) * mm, "end": v(-16.47, 46.5) * mm});
            skLineSegment(sketch, "E25.top", {"start": v(-70, 58.5) * mm, "end": v(-16.47, 58.5) * mm});
            skLineSegment(sketch, "E25.left", {"start": v(-70, 46.5) * mm, "end": v(-70, 58.5) * mm});
            skLineSegment(sketch, "E25.right", {"start": v(-16.47, 46.5) * mm, "end": v(-16.47, 58.5) * mm});
            skLineSegment(sketch, "E26.bottom", {"start": v(-70, 81.5) * mm, "end": v(-16.47, 81.5) * mm});
            skLineSegment(sketch, "E26.top", {"start": v(-70, 93.5) * mm, "end": v(-16.47, 93.5) * mm});
            skLineSegment(sketch, "E26.left", {"start": v(-70, 81.5) * mm, "end": v(-70, 93.5) * mm});
            skLineSegment(sketch, "E26.right", {"start": v(-16.47, 81.5) * mm, "end": v(-16.47, 93.5) * mm});
            skPoint(sketch, "E27", {"position": v(-75, 17.5) * mm});
            skPoint(sketch, "E28", {"position": v(-70, 17.5) * mm});
            skPoint(sketch, "E29", {"position": v(-70, 52.5) * mm});
            skPoint(sketch, "E30", {"position": v(-75, 52.5) * mm});
            skPoint(sketch, "E31", {"position": v(-75, 87.5) * mm});
            skPoint(sketch, "E32", {"position": v(-70, 87.5) * mm});
            skLineSegment(sketch, "E33", {"start": v(-16.47, 11.5) * mm, "end": v(-16.47, 101.43) * mm, "construction": true});
            skSolve(sketch);
        }
        {
            var Q0;
            Q0=makeQuery(id+"F13.imprint","IMPRINT",FACE,{"disambiguationData":[TD([[makeQuery(id+"F13.imprint","IMPRINT",EDGE,{"derivedFrom":sQuery(id+"F13.wireOp",EDGE,"E24.bottom")}),1.0]])]});
            var Q1;
            Q1=makeQuery(id+"F13.imprint","IMPRINT",FACE,{"disambiguationData":[TD([[makeQuery(id+"F13.imprint","IMPRINT",EDGE,{"derivedFrom":sQuery(id+"F13.wireOp",EDGE,"E25.bottom")}),1.0]])]});
            var Q2;
            Q2=makeQuery(id+"F13.imprint","IMPRINT",FACE,{"disambiguationData":[TD([[makeQuery(id+"F13.imprint","IMPRINT",EDGE,{"derivedFrom":sQuery(id+"F13.wireOp",EDGE,"E26.bottom")}),1.0]])]});
            extrude(context, id + "F14", {"entities" : qUnion([Q0, Q1, Q2]), "depth" : 2 * mm, "offsetDistance" : 25 * mm});
        }
        {
            var Q0;
            Q0=makeQuery(id+"F14.opExtrude","CAP_FACE",FACE,{"disambiguationData":[OSD([sQuery(id+"F13.wireOp",EDGE,"E24.bottom"),sQuery(id+"F13.wireOp",EDGE,"E24.top"),sQuery(id+"F13.wireOp",EDGE,"E24.left"),sQuery(id+"F13.wireOp",EDGE,"E24.right")])],"isStart":true});
            var sketch = newSketch(context, id + "F15", { "sketchPlane" : qUnion([Q0])});
            skText(sketch, "E34", { "text": "Brown 11mm\n", "fontName": "OpenSans-Bold.ttf"});
            skText(sketch, "E35", { "text": "Blue 10mm\n", "fontName": "OpenSans-Bold.ttf"});
            skText(sketch, "E36", { "text": "Green 9mm", "fontName": "OpenSans-Bold.ttf"});
            skLineSegment(sketch, "E37", {"start": v(20.47, 7.13) * mm, "end": v(20.47, 151.13) * mm, "construction": true});
            skPoint(sketch, "E37.endSnap0", {"position": v(20.47, 52.5) * mm});
            skPoint(sketch, "E38", {"position": v(61.86, 87.5) * mm});
            skPoint(sketch, "E39", {"position": v(62.15, 52.5) * mm});
            skPoint(sketch, "E40", {"position": v(67.58, 17.5) * mm});
            const initialGuessF15  = {"E34": [0.02047, 0.01494, 1, 0, 0.00513], "E35": [0.02047, 0.04981, 1, 0, 0.00538], "E36": [0.02047, 0.08493, 1, 0, 0.00514]};
            skSetInitialGuess(sketch, initialGuessF15);
            skSolve(sketch);
        }
        {
            var Q0;
            Q0 = qSketchRegion(id + "F15", true);
            extrude(context, id + "F16", {"entities" : qUnion([Q0]), "operationType" : NewBodyOperationType.REMOVE, "oppositeDirection" : true, "depth" : .2 * mm, "offsetDistance" : 25 * mm});
        }
        {
            var Q0;
            Q0=makeQuery(id+"F14.opExtrude","SWEPT_BODY",BODY,{"disambiguationData":[OSD([sQuery(id+"F13.wireOp",EDGE,"E24.bottom"),sQuery(id+"F13.wireOp",EDGE,"E24.top"),sQuery(id+"F13.wireOp",EDGE,"E24.left"),sQuery(id+"F13.wireOp",EDGE,"E24.right")])]});
            var Q1;
            Q1=makeQuery(id+"F14.opExtrude","SWEPT_BODY",BODY,{"disambiguationData":[OSD([sQuery(id+"F13.wireOp",EDGE,"E25.bottom"),sQuery(id+"F13.wireOp",EDGE,"E25.top"),sQuery(id+"F13.wireOp",EDGE,"E25.left"),sQuery(id+"F13.wireOp",EDGE,"E25.right")])]});
            var Q2;
            Q2=makeQuery(id+"F14.opExtrude","SWEPT_BODY",BODY,{"disambiguationData":[OSD([sQuery(id+"F13.wireOp",EDGE,"E26.bottom"),sQuery(id+"F13.wireOp",EDGE,"E26.top"),sQuery(id+"F13.wireOp",EDGE,"E26.left"),sQuery(id+"F13.wireOp",EDGE,"E26.right")])]});
            var Q3;
            Q3=makeQuery(id+"F14.opExtrude","SWEPT_EDGE",EDGE,{"disambiguationData":[OSD([sQuery(id+"F13.wireOp",EDGE,"E24.bottom"),sQuery(id+"F13.wireOp",EDGE,"E24.right")])]});
            transform(context, id + "F17", {"entities" : qUnion([Q0, Q1, Q2]), "transformType" : TransformType.ROTATION, "transformAxis" : qUnion([Q3]), "angle" : 180 * degree, "makeCopy" : false});
        }
        {
            var Q0;
            Q0=makeQuery(id+"F14.opExtrude","SWEPT_BODY",BODY,{"disambiguationData":[OSD([sQuery(id+"F13.wireOp",EDGE,"E26.bottom"),sQuery(id+"F13.wireOp",EDGE,"E26.top"),sQuery(id+"F13.wireOp",EDGE,"E26.left"),sQuery(id+"F13.wireOp",EDGE,"E26.right")])]});
            var Q1;
            Q1=makeQuery(id+"F14.opExtrude","SWEPT_BODY",BODY,{"disambiguationData":[OSD([sQuery(id+"F13.wireOp",EDGE,"E25.bottom"),sQuery(id+"F13.wireOp",EDGE,"E25.top"),sQuery(id+"F13.wireOp",EDGE,"E25.left"),sQuery(id+"F13.wireOp",EDGE,"E25.right")])]});
            var Q2;
            Q2=makeQuery(id+"F14.opExtrude","SWEPT_BODY",BODY,{"disambiguationData":[OSD([sQuery(id+"F13.wireOp",EDGE,"E24.bottom"),sQuery(id+"F13.wireOp",EDGE,"E24.top"),sQuery(id+"F13.wireOp",EDGE,"E24.left"),sQuery(id+"F13.wireOp",EDGE,"E24.right")])]});
            transform(context, id + "F18", {"entities" : qUnion([Q0, Q1, Q2]), "transformType" : TransformType.TRANSLATION_3D, "dx" : -53.5 * mm, "dy" : 0 * mm, "dz" : 81.9 * mm, "makeCopy" : false});
        }
        {
            var Q0;
            Q0=makeQuery(id+"F14.opExtrude","SWEPT_BODY",BODY,{"disambiguationData":[OSD([sQuery(id+"F13.wireOp",EDGE,"E26.bottom"),sQuery(id+"F13.wireOp",EDGE,"E26.top"),sQuery(id+"F13.wireOp",EDGE,"E26.left"),sQuery(id+"F13.wireOp",EDGE,"E26.right")])]});
            var Q1;
            Q1=makeQuery(id+"F1.opExtrude","SWEPT_BODY",BODY,{"disambiguationData":[OSD([sQuery(id+"F0.wireOp",EDGE,"E0"),sQuery(id+"F0.wireOp",EDGE,"E1.1.0.0"),sQuery(id+"F0.wireOp",EDGE,"E1.2.0.0"),sQuery(id+"F0.wireOp",EDGE,"E1.3.0.0"),sQuery(id+"F0.wireOp",EDGE,"E2"),sQuery(id+"F0.wireOp",EDGE,"E3.1.0.0"),sQuery(id+"F0.wireOp",EDGE,"E3.2.0.0"),sQuery(id+"F0.wireOp",EDGE,"E4"),sQuery(id+"F0.wireOp",EDGE,"E5.1.0.0"),sQuery(id+"F0.wireOp",EDGE,"E5.2.0.0"),sQuery(id+"F0.wireOp",EDGE,"E5.3.0.0"),sQuery(id+"F0.wireOp",EDGE,"E6"),sQuery(id+"F0.wireOp",EDGE,"E7.1.0.0"),sQuery(id+"F0.wireOp",EDGE,"E7.2.0.0")])]});
            var Q2;
            Q2=makeQuery(id+"F11.opExtrude","SWEPT_BODY",BODY,{"disambiguationData":[OSD([sQuery(id+"F9.wireOp",EDGE,"E10.sketch_text.stroke-0"),sQuery(id+"F9.wireOp",EDGE,"E10.sketch_text.stroke-1"),sQuery(id+"F9.wireOp",EDGE,"E10.sketch_text.stroke-2"),sQuery(id+"F9.wireOp",EDGE,"E10.sketch_text.stroke-3"),sQuery(id+"F9.wireOp",EDGE,"E10.sketch_text.stroke-4"),sQuery(id+"F9.wireOp",EDGE,"E10.sketch_text.stroke-5"),sQuery(id+"F9.wireOp",EDGE,"E10.sketch_text.stroke-6"),sQuery(id+"F9.wireOp",EDGE,"E10.sketch_text.stroke-7"),sQuery(id+"F9.wireOp",EDGE,"E10.sketch_text.stroke-8"),sQuery(id+"F9.wireOp",EDGE,"E10.sketch_text.stroke-9"),sQuery(id+"F9.wireOp",EDGE,"E10.sketch_text.stroke-10"),sQuery(id+"F9.wireOp",EDGE,"E10.sketch_text.stroke-11"),sQuery(id+"F9.wireOp",EDGE,"E10.sketch_text.stroke-12"),sQuery(id+"F9.wireOp",EDGE,"E10.sketch_text.stroke-13"),sQuery(id+"F9.wireOp",EDGE,"E10.sketch_text.stroke-14"),sQuery(id+"F9.wireOp",EDGE,"E10.sketch_text.stroke-15"),sQuery(id+"F9.wireOp",EDGE,"E10.sketch_text.stroke-16"),sQuery(id+"F9.wireOp",EDGE,"E10.sketch_text.stroke-17"),sQuery(id+"F9.wireOp",EDGE,"E10.sketch_text.stroke-18"),sQuery(id+"F9.wireOp",EDGE,"E10.sketch_text.stroke-19"),sQuery(id+"F9.wireOp",EDGE,"E10.sketch_text.stroke-20"),sQuery(id+"F9.wireOp",EDGE,"E10.sketch_text.stroke-21"),sQuery(id+"F9.wireOp",EDGE,"E10.sketch_text.stroke-22"),sQuery(id+"F9.wireOp",EDGE,"E10.sketch_text.stroke-23"),sQuery(id+"F9.wireOp",EDGE,"E10.sketch_text.stroke-24")])]});
            var Q3;
            Q3=makeQuery(id+"F11.opExtrude","SWEPT_BODY",BODY,{"disambiguationData":[OSD([sQuery(id+"F9.wireOp",EDGE,"E10.sketch_text.stroke-25"),sQuery(id+"F9.wireOp",EDGE,"E10.sketch_text.stroke-26"),sQuery(id+"F9.wireOp",EDGE,"E10.sketch_text.stroke-27"),sQuery(id+"F9.wireOp",EDGE,"E10.sketch_text.stroke-28")])]});
            var Q4;
            Q4=makeQuery(id+"F11.opExtrude","SWEPT_BODY",BODY,{"disambiguationData":[OSD([sQuery(id+"F9.wireOp",EDGE,"E10.sketch_text.stroke-29"),sQuery(id+"F9.wireOp",EDGE,"E10.sketch_text.stroke-30"),sQuery(id+"F9.wireOp",EDGE,"E10.sketch_text.stroke-31"),sQuery(id+"F9.wireOp",EDGE,"E10.sketch_text.stroke-32"),sQuery(id+"F9.wireOp",EDGE,"E10.sketch_text.stroke-33"),sQuery(id+"F9.wireOp",EDGE,"E10.sketch_text.stroke-34"),sQuery(id+"F9.wireOp",EDGE,"E10.sketch_text.stroke-35"),sQuery(id+"F9.wireOp",EDGE,"E10.sketch_text.stroke-36"),sQuery(id+"F9.wireOp",EDGE,"E10.sketch_text.stroke-37"),sQuery(id+"F9.wireOp",EDGE,"E10.sketch_text.stroke-38"),sQuery(id+"F9.wireOp",EDGE,"E10.sketch_text.stroke-39"),sQuery(id+"F9.wireOp",EDGE,"E10.sketch_text.stroke-40"),sQuery(id+"F9.wireOp",EDGE,"E10.sketch_text.stroke-41"),sQuery(id+"F9.wireOp",EDGE,"E10.sketch_text.stroke-42"),sQuery(id+"F9.wireOp",EDGE,"E10.sketch_text.stroke-43"),sQuery(id+"F9.wireOp",EDGE,"E10.sketch_text.stroke-44"),sQuery(id+"F9.wireOp",EDGE,"E10.sketch_text.stroke-45"),sQuery(id+"F9.wireOp",EDGE,"E10.sketch_text.stroke-46"),sQuery(id+"F9.wireOp",EDGE,"E10.sketch_text.stroke-47"),sQuery(id+"F9.wireOp",EDGE,"E10.sketch_text.stroke-48"),sQuery(id+"F9.wireOp",EDGE,"E10.sketch_text.stroke-49"),sQuery(id+"F9.wireOp",EDGE,"E10.sketch_text.stroke-50"),sQuery(id+"F9.wireOp",EDGE,"E10.sketch_text.stroke-51"),sQuery(id+"F9.wireOp",EDGE,"E10.sketch_text.stroke-52"),sQuery(id+"F9.wireOp",EDGE,"E10.sketch_text.stroke-53")])]});
            var Q5;
            Q5=makeQuery(id+"F11.opExtrude","SWEPT_BODY",BODY,{"disambiguationData":[OSD([sQuery(id+"F9.wireOp",EDGE,"E10.sketch_text.stroke-54"),sQuery(id+"F9.wireOp",EDGE,"E10.sketch_text.stroke-55"),sQuery(id+"F9.wireOp",EDGE,"E10.sketch_text.stroke-56"),sQuery(id+"F9.wireOp",EDGE,"E10.sketch_text.stroke-57"),sQuery(id+"F9.wireOp",EDGE,"E10.sketch_text.stroke-58"),sQuery(id+"F9.wireOp",EDGE,"E10.sketch_text.stroke-59"),sQuery(id+"F9.wireOp",EDGE,"E10.sketch_text.stroke-60"),sQuery(id+"F9.wireOp",EDGE,"E10.sketch_text.stroke-61"),sQuery(id+"F9.wireOp",EDGE,"E10.sketch_text.stroke-62"),sQuery(id+"F9.wireOp",EDGE,"E10.sketch_text.stroke-63"),sQuery(id+"F9.wireOp",EDGE,"E10.sketch_text.stroke-64"),sQuery(id+"F9.wireOp",EDGE,"E10.sketch_text.stroke-65"),sQuery(id+"F9.wireOp",EDGE,"E10.sketch_text.stroke-66"),sQuery(id+"F9.wireOp",EDGE,"E10.sketch_text.stroke-67")])]});
            var Q6;
            Q6=makeQuery(id+"F11.opExtrude","SWEPT_BODY",BODY,{"disambiguationData":[OSD([sQuery(id+"F9.wireOp",EDGE,"E10.sketch_text.stroke-68"),sQuery(id+"F9.wireOp",EDGE,"E10.sketch_text.stroke-69"),sQuery(id+"F9.wireOp",EDGE,"E10.sketch_text.stroke-70"),sQuery(id+"F9.wireOp",EDGE,"E10.sketch_text.stroke-71"),sQuery(id+"F9.wireOp",EDGE,"E10.sketch_text.stroke-72"),sQuery(id+"F9.wireOp",EDGE,"E10.sketch_text.stroke-73"),sQuery(id+"F9.wireOp",EDGE,"E10.sketch_text.stroke-74"),sQuery(id+"F9.wireOp",EDGE,"E10.sketch_text.stroke-75"),sQuery(id+"F9.wireOp",EDGE,"E10.sketch_text.stroke-76"),sQuery(id+"F9.wireOp",EDGE,"E10.sketch_text.stroke-77"),sQuery(id+"F9.wireOp",EDGE,"E10.sketch_text.stroke-78"),sQuery(id+"F9.wireOp",EDGE,"E10.sketch_text.stroke-79"),sQuery(id+"F9.wireOp",EDGE,"E10.sketch_text.stroke-80"),sQuery(id+"F9.wireOp",EDGE,"E10.sketch_text.stroke-81"),sQuery(id+"F9.wireOp",EDGE,"E10.sketch_text.stroke-82")])]});
            var Q7;
            Q7=makeQuery(id+"F11.opExtrude","SWEPT_BODY",BODY,{"disambiguationData":[OSD([sQuery(id+"F9.wireOp",EDGE,"E10.sketch_text.stroke-83"),sQuery(id+"F9.wireOp",EDGE,"E10.sketch_text.stroke-84"),sQuery(id+"F9.wireOp",EDGE,"E10.sketch_text.stroke-85"),sQuery(id+"F9.wireOp",EDGE,"E10.sketch_text.stroke-86"),sQuery(id+"F9.wireOp",EDGE,"E10.sketch_text.stroke-87"),sQuery(id+"F9.wireOp",EDGE,"E10.sketch_text.stroke-88"),sQuery(id+"F9.wireOp",EDGE,"E10.sketch_text.stroke-89"),sQuery(id+"F9.wireOp",EDGE,"E10.sketch_text.stroke-90"),sQuery(id+"F9.wireOp",EDGE,"E10.sketch_text.stroke-91"),sQuery(id+"F9.wireOp",EDGE,"E10.sketch_text.stroke-92"),sQuery(id+"F9.wireOp",EDGE,"E10.sketch_text.stroke-93"),sQuery(id+"F9.wireOp",EDGE,"E10.sketch_text.stroke-94"),sQuery(id+"F9.wireOp",EDGE,"E10.sketch_text.stroke-95"),sQuery(id+"F9.wireOp",EDGE,"E10.sketch_text.stroke-96"),sQuery(id+"F9.wireOp",EDGE,"E10.sketch_text.stroke-97"),sQuery(id+"F9.wireOp",EDGE,"E10.sketch_text.stroke-98"),sQuery(id+"F9.wireOp",EDGE,"E10.sketch_text.stroke-99"),sQuery(id+"F9.wireOp",EDGE,"E10.sketch_text.stroke-100"),sQuery(id+"F9.wireOp",EDGE,"E10.sketch_text.stroke-101"),sQuery(id+"F9.wireOp",EDGE,"E10.sketch_text.stroke-102")])]});
            var Q8;
            Q8=makeQuery(id+"F11.opExtrude","SWEPT_BODY",BODY,{"disambiguationData":[OSD([sQuery(id+"F9.wireOp",EDGE,"E10.sketch_text.stroke-103"),sQuery(id+"F9.wireOp",EDGE,"E10.sketch_text.stroke-104"),sQuery(id+"F9.wireOp",EDGE,"E10.sketch_text.stroke-105"),sQuery(id+"F9.wireOp",EDGE,"E10.sketch_text.stroke-106"),sQuery(id+"F9.wireOp",EDGE,"E10.sketch_text.stroke-107"),sQuery(id+"F9.wireOp",EDGE,"E10.sketch_text.stroke-108"),sQuery(id+"F9.wireOp",EDGE,"E10.sketch_text.stroke-109"),sQuery(id+"F9.wireOp",EDGE,"E10.sketch_text.stroke-110"),sQuery(id+"F9.wireOp",EDGE,"E10.sketch_text.stroke-111"),sQuery(id+"F9.wireOp",EDGE,"E10.sketch_text.stroke-112"),sQuery(id+"F9.wireOp",EDGE,"E10.sketch_text.stroke-113"),sQuery(id+"F9.wireOp",EDGE,"E10.sketch_text.stroke-114"),sQuery(id+"F9.wireOp",EDGE,"E10.sketch_text.stroke-115"),sQuery(id+"F9.wireOp",EDGE,"E10.sketch_text.stroke-116"),sQuery(id+"F9.wireOp",EDGE,"E10.sketch_text.stroke-117"),sQuery(id+"F9.wireOp",EDGE,"E10.sketch_text.stroke-118"),sQuery(id+"F9.wireOp",EDGE,"E10.sketch_text.stroke-119"),sQuery(id+"F9.wireOp",EDGE,"E10.sketch_text.stroke-120"),sQuery(id+"F9.wireOp",EDGE,"E10.sketch_text.stroke-121"),sQuery(id+"F9.wireOp",EDGE,"E10.sketch_text.stroke-122"),sQuery(id+"F9.wireOp",EDGE,"E10.sketch_text.stroke-123"),sQuery(id+"F9.wireOp",EDGE,"E10.sketch_text.stroke-124"),sQuery(id+"F9.wireOp",EDGE,"E10.sketch_text.stroke-125"),sQuery(id+"F9.wireOp",EDGE,"E10.sketch_text.stroke-126"),sQuery(id+"F9.wireOp",EDGE,"E10.sketch_text.stroke-127"),sQuery(id+"F9.wireOp",EDGE,"E10.sketch_text.stroke-128"),sQuery(id+"F9.wireOp",EDGE,"E10.sketch_text.stroke-129"),sQuery(id+"F9.wireOp",EDGE,"E10.sketch_text.stroke-130")])]});
            var Q9;
            Q9=makeQuery(id+"F11.opExtrude","SWEPT_BODY",BODY,{"disambiguationData":[OSD([sQuery(id+"F9.wireOp",EDGE,"E10.sketch_text.stroke-131"),sQuery(id+"F9.wireOp",EDGE,"E10.sketch_text.stroke-132"),sQuery(id+"F9.wireOp",EDGE,"E10.sketch_text.stroke-133"),sQuery(id+"F9.wireOp",EDGE,"E10.sketch_text.stroke-134"),sQuery(id+"F9.wireOp",EDGE,"E10.sketch_text.stroke-135"),sQuery(id+"F9.wireOp",EDGE,"E10.sketch_text.stroke-136"),sQuery(id+"F9.wireOp",EDGE,"E10.sketch_text.stroke-137"),sQuery(id+"F9.wireOp",EDGE,"E10.sketch_text.stroke-138"),sQuery(id+"F9.wireOp",EDGE,"E10.sketch_text.stroke-139"),sQuery(id+"F9.wireOp",EDGE,"E10.sketch_text.stroke-140"),sQuery(id+"F9.wireOp",EDGE,"E10.sketch_text.stroke-141"),sQuery(id+"F9.wireOp",EDGE,"E10.sketch_text.stroke-142"),sQuery(id+"F9.wireOp",EDGE,"E10.sketch_text.stroke-143"),sQuery(id+"F9.wireOp",EDGE,"E10.sketch_text.stroke-144"),sQuery(id+"F9.wireOp",EDGE,"E10.sketch_text.stroke-145"),sQuery(id+"F9.wireOp",EDGE,"E10.sketch_text.stroke-146"),sQuery(id+"F9.wireOp",EDGE,"E10.sketch_text.stroke-147"),sQuery(id+"F9.wireOp",EDGE,"E10.sketch_text.stroke-148"),sQuery(id+"F9.wireOp",EDGE,"E10.sketch_text.stroke-149"),sQuery(id+"F9.wireOp",EDGE,"E10.sketch_text.stroke-150"),sQuery(id+"F9.wireOp",EDGE,"E10.sketch_text.stroke-151"),sQuery(id+"F9.wireOp",EDGE,"E10.sketch_text.stroke-152"),sQuery(id+"F9.wireOp",EDGE,"E10.sketch_text.stroke-153"),sQuery(id+"F9.wireOp",EDGE,"E10.sketch_text.stroke-154"),sQuery(id+"F9.wireOp",EDGE,"E10.sketch_text.stroke-155"),sQuery(id+"F9.wireOp",EDGE,"E10.sketch_text.stroke-156"),sQuery(id+"F9.wireOp",EDGE,"E10.sketch_text.stroke-157"),sQuery(id+"F9.wireOp",EDGE,"E10.sketch_text.stroke-158")])]});
            var Q10;
            Q10=makeQuery(id+"F11.opExtrude","SWEPT_BODY",BODY,{"disambiguationData":[OSD([sQuery(id+"F9.wireOp",EDGE,"E11.sketch_text.stroke-0"),sQuery(id+"F9.wireOp",EDGE,"E11.sketch_text.stroke-1"),sQuery(id+"F9.wireOp",EDGE,"E11.sketch_text.stroke-2"),sQuery(id+"F9.wireOp",EDGE,"E11.sketch_text.stroke-3"),sQuery(id+"F9.wireOp",EDGE,"E11.sketch_text.stroke-4"),sQuery(id+"F9.wireOp",EDGE,"E11.sketch_text.stroke-5"),sQuery(id+"F9.wireOp",EDGE,"E11.sketch_text.stroke-6"),sQuery(id+"F9.wireOp",EDGE,"E11.sketch_text.stroke-7"),sQuery(id+"F9.wireOp",EDGE,"E11.sketch_text.stroke-8"),sQuery(id+"F9.wireOp",EDGE,"E11.sketch_text.stroke-9"),sQuery(id+"F9.wireOp",EDGE,"E11.sketch_text.stroke-10"),sQuery(id+"F9.wireOp",EDGE,"E11.sketch_text.stroke-11"),sQuery(id+"F9.wireOp",EDGE,"E11.sketch_text.stroke-12"),sQuery(id+"F9.wireOp",EDGE,"E11.sketch_text.stroke-13"),sQuery(id+"F9.wireOp",EDGE,"E11.sketch_text.stroke-14"),sQuery(id+"F9.wireOp",EDGE,"E11.sketch_text.stroke-15"),sQuery(id+"F9.wireOp",EDGE,"E11.sketch_text.stroke-16"),sQuery(id+"F9.wireOp",EDGE,"E11.sketch_text.stroke-17")])]});
            var Q11;
            Q11=makeQuery(id+"F11.opExtrude","SWEPT_BODY",BODY,{"disambiguationData":[OSD([sQuery(id+"F9.wireOp",EDGE,"E11.sketch_text.stroke-18"),sQuery(id+"F9.wireOp",EDGE,"E11.sketch_text.stroke-19"),sQuery(id+"F9.wireOp",EDGE,"E11.sketch_text.stroke-20"),sQuery(id+"F9.wireOp",EDGE,"E11.sketch_text.stroke-21"),sQuery(id+"F9.wireOp",EDGE,"E11.sketch_text.stroke-22"),sQuery(id+"F9.wireOp",EDGE,"E11.sketch_text.stroke-23"),sQuery(id+"F9.wireOp",EDGE,"E11.sketch_text.stroke-24"),sQuery(id+"F9.wireOp",EDGE,"E11.sketch_text.stroke-25"),sQuery(id+"F9.wireOp",EDGE,"E11.sketch_text.stroke-26"),sQuery(id+"F9.wireOp",EDGE,"E11.sketch_text.stroke-27"),sQuery(id+"F9.wireOp",EDGE,"E11.sketch_text.stroke-28"),sQuery(id+"F9.wireOp",EDGE,"E11.sketch_text.stroke-29"),sQuery(id+"F9.wireOp",EDGE,"E11.sketch_text.stroke-30"),sQuery(id+"F9.wireOp",EDGE,"E11.sketch_text.stroke-31"),sQuery(id+"F9.wireOp",EDGE,"E11.sketch_text.stroke-32"),sQuery(id+"F9.wireOp",EDGE,"E11.sketch_text.stroke-33"),sQuery(id+"F9.wireOp",EDGE,"E11.sketch_text.stroke-34"),sQuery(id+"F9.wireOp",EDGE,"E11.sketch_text.stroke-35"),sQuery(id+"F9.wireOp",EDGE,"E11.sketch_text.stroke-36")])]});
            var Q12;
            Q12=makeQuery(id+"F11.opExtrude","SWEPT_BODY",BODY,{"disambiguationData":[OSD([sQuery(id+"F9.wireOp",EDGE,"E11.sketch_text.stroke-37"),sQuery(id+"F9.wireOp",EDGE,"E11.sketch_text.stroke-38"),sQuery(id+"F9.wireOp",EDGE,"E11.sketch_text.stroke-39"),sQuery(id+"F9.wireOp",EDGE,"E11.sketch_text.stroke-40"),sQuery(id+"F9.wireOp",EDGE,"E11.sketch_text.stroke-41"),sQuery(id+"F9.wireOp",EDGE,"E11.sketch_text.stroke-42"),sQuery(id+"F9.wireOp",EDGE,"E11.sketch_text.stroke-43"),sQuery(id+"F9.wireOp",EDGE,"E11.sketch_text.stroke-44"),sQuery(id+"F9.wireOp",EDGE,"E11.sketch_text.stroke-45"),sQuery(id+"F9.wireOp",EDGE,"E11.sketch_text.stroke-46"),sQuery(id+"F9.wireOp",EDGE,"E11.sketch_text.stroke-47"),sQuery(id+"F9.wireOp",EDGE,"E11.sketch_text.stroke-48"),sQuery(id+"F9.wireOp",EDGE,"E11.sketch_text.stroke-49"),sQuery(id+"F9.wireOp",EDGE,"E11.sketch_text.stroke-50"),sQuery(id+"F9.wireOp",EDGE,"E11.sketch_text.stroke-51"),sQuery(id+"F9.wireOp",EDGE,"E11.sketch_text.stroke-52"),sQuery(id+"F9.wireOp",EDGE,"E11.sketch_text.stroke-53"),sQuery(id+"F9.wireOp",EDGE,"E11.sketch_text.stroke-54"),sQuery(id+"F9.wireOp",EDGE,"E11.sketch_text.stroke-55"),sQuery(id+"F9.wireOp",EDGE,"E11.sketch_text.stroke-56"),sQuery(id+"F9.wireOp",EDGE,"E11.sketch_text.stroke-57"),sQuery(id+"F9.wireOp",EDGE,"E11.sketch_text.stroke-58"),sQuery(id+"F9.wireOp",EDGE,"E11.sketch_text.stroke-59"),sQuery(id+"F9.wireOp",EDGE,"E11.sketch_text.stroke-60")])]});
            var Q13;
            Q13=makeQuery(id+"F11.opExtrude","SWEPT_BODY",BODY,{"disambiguationData":[OSD([sQuery(id+"F9.wireOp",EDGE,"E11.sketch_text.stroke-61"),sQuery(id+"F9.wireOp",EDGE,"E11.sketch_text.stroke-62"),sQuery(id+"F9.wireOp",EDGE,"E11.sketch_text.stroke-63"),sQuery(id+"F9.wireOp",EDGE,"E11.sketch_text.stroke-64"),sQuery(id+"F9.wireOp",EDGE,"E11.sketch_text.stroke-65"),sQuery(id+"F9.wireOp",EDGE,"E11.sketch_text.stroke-66"),sQuery(id+"F9.wireOp",EDGE,"E11.sketch_text.stroke-67"),sQuery(id+"F9.wireOp",EDGE,"E11.sketch_text.stroke-68"),sQuery(id+"F9.wireOp",EDGE,"E11.sketch_text.stroke-69"),sQuery(id+"F9.wireOp",EDGE,"E11.sketch_text.stroke-70"),sQuery(id+"F9.wireOp",EDGE,"E11.sketch_text.stroke-71"),sQuery(id+"F9.wireOp",EDGE,"E11.sketch_text.stroke-72"),sQuery(id+"F9.wireOp",EDGE,"E11.sketch_text.stroke-73"),sQuery(id+"F9.wireOp",EDGE,"E11.sketch_text.stroke-74"),sQuery(id+"F9.wireOp",EDGE,"E11.sketch_text.stroke-75"),sQuery(id+"F9.wireOp",EDGE,"E11.sketch_text.stroke-76"),sQuery(id+"F9.wireOp",EDGE,"E11.sketch_text.stroke-77"),sQuery(id+"F9.wireOp",EDGE,"E11.sketch_text.stroke-78"),sQuery(id+"F9.wireOp",EDGE,"E11.sketch_text.stroke-79"),sQuery(id+"F9.wireOp",EDGE,"E11.sketch_text.stroke-80"),sQuery(id+"F9.wireOp",EDGE,"E11.sketch_text.stroke-81"),sQuery(id+"F9.wireOp",EDGE,"E11.sketch_text.stroke-82"),sQuery(id+"F9.wireOp",EDGE,"E11.sketch_text.stroke-83"),sQuery(id+"F9.wireOp",EDGE,"E11.sketch_text.stroke-84"),sQuery(id+"F9.wireOp",EDGE,"E11.sketch_text.stroke-85")])]});
            var Q14;
            Q14=makeQuery(id+"F11.opExtrude","SWEPT_BODY",BODY,{"disambiguationData":[OSD([sQuery(id+"F9.wireOp",EDGE,"E11.sketch_text.stroke-86"),sQuery(id+"F9.wireOp",EDGE,"E11.sketch_text.stroke-87"),sQuery(id+"F9.wireOp",EDGE,"E11.sketch_text.stroke-88"),sQuery(id+"F9.wireOp",EDGE,"E11.sketch_text.stroke-89"),sQuery(id+"F9.wireOp",EDGE,"E11.sketch_text.stroke-90"),sQuery(id+"F9.wireOp",EDGE,"E11.sketch_text.stroke-91"),sQuery(id+"F9.wireOp",EDGE,"E11.sketch_text.stroke-92"),sQuery(id+"F9.wireOp",EDGE,"E11.sketch_text.stroke-93"),sQuery(id+"F9.wireOp",EDGE,"E11.sketch_text.stroke-94"),sQuery(id+"F9.wireOp",EDGE,"E11.sketch_text.stroke-95"),sQuery(id+"F9.wireOp",EDGE,"E11.sketch_text.stroke-96"),sQuery(id+"F9.wireOp",EDGE,"E11.sketch_text.stroke-97"),sQuery(id+"F9.wireOp",EDGE,"E11.sketch_text.stroke-98"),sQuery(id+"F9.wireOp",EDGE,"E11.sketch_text.stroke-99"),sQuery(id+"F9.wireOp",EDGE,"E11.sketch_text.stroke-100"),sQuery(id+"F9.wireOp",EDGE,"E11.sketch_text.stroke-101"),sQuery(id+"F9.wireOp",EDGE,"E11.sketch_text.stroke-102"),sQuery(id+"F9.wireOp",EDGE,"E11.sketch_text.stroke-103"),sQuery(id+"F9.wireOp",EDGE,"E11.sketch_text.stroke-104"),sQuery(id+"F9.wireOp",EDGE,"E11.sketch_text.stroke-105"),sQuery(id+"F9.wireOp",EDGE,"E11.sketch_text.stroke-106"),sQuery(id+"F9.wireOp",EDGE,"E11.sketch_text.stroke-107"),sQuery(id+"F9.wireOp",EDGE,"E11.sketch_text.stroke-108"),sQuery(id+"F9.wireOp",EDGE,"E11.sketch_text.stroke-109"),sQuery(id+"F9.wireOp",EDGE,"E11.sketch_text.stroke-110"),sQuery(id+"F9.wireOp",EDGE,"E11.sketch_text.stroke-111"),sQuery(id+"F9.wireOp",EDGE,"E11.sketch_text.stroke-112"),sQuery(id+"F9.wireOp",EDGE,"E11.sketch_text.stroke-113")])]});
            var Q15;
            Q15=makeQuery(id+"F11.opExtrude","SWEPT_BODY",BODY,{"disambiguationData":[OSD([sQuery(id+"F9.wireOp",EDGE,"E11.sketch_text.stroke-114"),sQuery(id+"F9.wireOp",EDGE,"E11.sketch_text.stroke-115"),sQuery(id+"F9.wireOp",EDGE,"E11.sketch_text.stroke-116"),sQuery(id+"F9.wireOp",EDGE,"E11.sketch_text.stroke-117"),sQuery(id+"F9.wireOp",EDGE,"E11.sketch_text.stroke-118"),sQuery(id+"F9.wireOp",EDGE,"E11.sketch_text.stroke-119"),sQuery(id+"F9.wireOp",EDGE,"E11.sketch_text.stroke-120"),sQuery(id+"F9.wireOp",EDGE,"E11.sketch_text.stroke-121"),sQuery(id+"F9.wireOp",EDGE,"E11.sketch_text.stroke-122"),sQuery(id+"F9.wireOp",EDGE,"E11.sketch_text.stroke-123"),sQuery(id+"F9.wireOp",EDGE,"E11.sketch_text.stroke-124"),sQuery(id+"F9.wireOp",EDGE,"E11.sketch_text.stroke-125"),sQuery(id+"F9.wireOp",EDGE,"E11.sketch_text.stroke-126"),sQuery(id+"F9.wireOp",EDGE,"E11.sketch_text.stroke-127"),sQuery(id+"F9.wireOp",EDGE,"E11.sketch_text.stroke-128"),sQuery(id+"F9.wireOp",EDGE,"E11.sketch_text.stroke-129"),sQuery(id+"F9.wireOp",EDGE,"E11.sketch_text.stroke-130"),sQuery(id+"F9.wireOp",EDGE,"E11.sketch_text.stroke-131"),sQuery(id+"F9.wireOp",EDGE,"E11.sketch_text.stroke-132"),sQuery(id+"F9.wireOp",EDGE,"E11.sketch_text.stroke-133"),sQuery(id+"F9.wireOp",EDGE,"E11.sketch_text.stroke-134"),sQuery(id+"F9.wireOp",EDGE,"E11.sketch_text.stroke-135"),sQuery(id+"F9.wireOp",EDGE,"E11.sketch_text.stroke-136"),sQuery(id+"F9.wireOp",EDGE,"E11.sketch_text.stroke-137"),sQuery(id+"F9.wireOp",EDGE,"E11.sketch_text.stroke-138"),sQuery(id+"F9.wireOp",EDGE,"E11.sketch_text.stroke-139"),sQuery(id+"F9.wireOp",EDGE,"E11.sketch_text.stroke-140"),sQuery(id+"F9.wireOp",EDGE,"E11.sketch_text.stroke-141")])]});
            var Q16;
            Q16=makeQuery(id+"F11.opExtrude","SWEPT_BODY",BODY,{"disambiguationData":[OSD([sQuery(id+"F9.wireOp",EDGE,"E12.sketch_text.stroke-0"),sQuery(id+"F9.wireOp",EDGE,"E12.sketch_text.stroke-1"),sQuery(id+"F9.wireOp",EDGE,"E12.sketch_text.stroke-2"),sQuery(id+"F9.wireOp",EDGE,"E12.sketch_text.stroke-3"),sQuery(id+"F9.wireOp",EDGE,"E12.sketch_text.stroke-4"),sQuery(id+"F9.wireOp",EDGE,"E12.sketch_text.stroke-5"),sQuery(id+"F9.wireOp",EDGE,"E12.sketch_text.stroke-6"),sQuery(id+"F9.wireOp",EDGE,"E12.sketch_text.stroke-7"),sQuery(id+"F9.wireOp",EDGE,"E12.sketch_text.stroke-8"),sQuery(id+"F9.wireOp",EDGE,"E12.sketch_text.stroke-9"),sQuery(id+"F9.wireOp",EDGE,"E12.sketch_text.stroke-10"),sQuery(id+"F9.wireOp",EDGE,"E12.sketch_text.stroke-11"),sQuery(id+"F9.wireOp",EDGE,"E12.sketch_text.stroke-12"),sQuery(id+"F9.wireOp",EDGE,"E12.sketch_text.stroke-13"),sQuery(id+"F9.wireOp",EDGE,"E12.sketch_text.stroke-14"),sQuery(id+"F9.wireOp",EDGE,"E12.sketch_text.stroke-15")])]});
            var Q17;
            Q17=makeQuery(id+"F11.opExtrude","SWEPT_BODY",BODY,{"disambiguationData":[OSD([sQuery(id+"F9.wireOp",EDGE,"E12.sketch_text.stroke-16"),sQuery(id+"F9.wireOp",EDGE,"E12.sketch_text.stroke-17"),sQuery(id+"F9.wireOp",EDGE,"E12.sketch_text.stroke-18"),sQuery(id+"F9.wireOp",EDGE,"E12.sketch_text.stroke-19"),sQuery(id+"F9.wireOp",EDGE,"E12.sketch_text.stroke-20"),sQuery(id+"F9.wireOp",EDGE,"E12.sketch_text.stroke-21"),sQuery(id+"F9.wireOp",EDGE,"E12.sketch_text.stroke-22"),sQuery(id+"F9.wireOp",EDGE,"E12.sketch_text.stroke-23"),sQuery(id+"F9.wireOp",EDGE,"E12.sketch_text.stroke-24"),sQuery(id+"F9.wireOp",EDGE,"E12.sketch_text.stroke-25"),sQuery(id+"F9.wireOp",EDGE,"E12.sketch_text.stroke-26"),sQuery(id+"F9.wireOp",EDGE,"E12.sketch_text.stroke-27"),sQuery(id+"F9.wireOp",EDGE,"E12.sketch_text.stroke-28")])]});
            var Q18;
            Q18=makeQuery(id+"F11.opExtrude","SWEPT_BODY",BODY,{"disambiguationData":[OSD([sQuery(id+"F9.wireOp",EDGE,"E12.sketch_text.stroke-29"),sQuery(id+"F9.wireOp",EDGE,"E12.sketch_text.stroke-30"),sQuery(id+"F9.wireOp",EDGE,"E12.sketch_text.stroke-31"),sQuery(id+"F9.wireOp",EDGE,"E12.sketch_text.stroke-32"),sQuery(id+"F9.wireOp",EDGE,"E12.sketch_text.stroke-33"),sQuery(id+"F9.wireOp",EDGE,"E12.sketch_text.stroke-34"),sQuery(id+"F9.wireOp",EDGE,"E12.sketch_text.stroke-35"),sQuery(id+"F9.wireOp",EDGE,"E12.sketch_text.stroke-36"),sQuery(id+"F9.wireOp",EDGE,"E12.sketch_text.stroke-37"),sQuery(id+"F9.wireOp",EDGE,"E12.sketch_text.stroke-38"),sQuery(id+"F9.wireOp",EDGE,"E12.sketch_text.stroke-39"),sQuery(id+"F9.wireOp",EDGE,"E12.sketch_text.stroke-40"),sQuery(id+"F9.wireOp",EDGE,"E12.sketch_text.stroke-41"),sQuery(id+"F9.wireOp",EDGE,"E12.sketch_text.stroke-42"),sQuery(id+"F9.wireOp",EDGE,"E12.sketch_text.stroke-43"),sQuery(id+"F9.wireOp",EDGE,"E12.sketch_text.stroke-44"),sQuery(id+"F9.wireOp",EDGE,"E12.sketch_text.stroke-45"),sQuery(id+"F9.wireOp",EDGE,"E12.sketch_text.stroke-46"),sQuery(id+"F9.wireOp",EDGE,"E12.sketch_text.stroke-47"),sQuery(id+"F9.wireOp",EDGE,"E12.sketch_text.stroke-48"),sQuery(id+"F9.wireOp",EDGE,"E12.sketch_text.stroke-49"),sQuery(id+"F9.wireOp",EDGE,"E12.sketch_text.stroke-50"),sQuery(id+"F9.wireOp",EDGE,"E12.sketch_text.stroke-51"),sQuery(id+"F9.wireOp",EDGE,"E12.sketch_text.stroke-52"),sQuery(id+"F9.wireOp",EDGE,"E12.sketch_text.stroke-53"),sQuery(id+"F9.wireOp",EDGE,"E12.sketch_text.stroke-54"),sQuery(id+"F9.wireOp",EDGE,"E12.sketch_text.stroke-55")])]});
            var Q19;
            Q19=makeQuery(id+"F11.opExtrude","SWEPT_BODY",BODY,{"disambiguationData":[OSD([sQuery(id+"F9.wireOp",EDGE,"E12.sketch_text.stroke-56"),sQuery(id+"F9.wireOp",EDGE,"E12.sketch_text.stroke-57"),sQuery(id+"F9.wireOp",EDGE,"E12.sketch_text.stroke-58"),sQuery(id+"F9.wireOp",EDGE,"E12.sketch_text.stroke-59"),sQuery(id+"F9.wireOp",EDGE,"E12.sketch_text.stroke-60"),sQuery(id+"F9.wireOp",EDGE,"E12.sketch_text.stroke-61"),sQuery(id+"F9.wireOp",EDGE,"E12.sketch_text.stroke-62"),sQuery(id+"F9.wireOp",EDGE,"E12.sketch_text.stroke-63"),sQuery(id+"F9.wireOp",EDGE,"E12.sketch_text.stroke-64"),sQuery(id+"F9.wireOp",EDGE,"E12.sketch_text.stroke-65"),sQuery(id+"F9.wireOp",EDGE,"E12.sketch_text.stroke-66"),sQuery(id+"F9.wireOp",EDGE,"E12.sketch_text.stroke-67"),sQuery(id+"F9.wireOp",EDGE,"E12.sketch_text.stroke-68"),sQuery(id+"F9.wireOp",EDGE,"E12.sketch_text.stroke-69"),sQuery(id+"F9.wireOp",EDGE,"E12.sketch_text.stroke-70"),sQuery(id+"F9.wireOp",EDGE,"E12.sketch_text.stroke-71"),sQuery(id+"F9.wireOp",EDGE,"E12.sketch_text.stroke-72")])]});
            var Q20;
            Q20=makeQuery(id+"F11.opExtrude","SWEPT_BODY",BODY,{"disambiguationData":[OSD([sQuery(id+"F9.wireOp",EDGE,"E12.sketch_text.stroke-73"),sQuery(id+"F9.wireOp",EDGE,"E12.sketch_text.stroke-74"),sQuery(id+"F9.wireOp",EDGE,"E12.sketch_text.stroke-75"),sQuery(id+"F9.wireOp",EDGE,"E12.sketch_text.stroke-76"),sQuery(id+"F9.wireOp",EDGE,"E12.sketch_text.stroke-77"),sQuery(id+"F9.wireOp",EDGE,"E12.sketch_text.stroke-78"),sQuery(id+"F9.wireOp",EDGE,"E12.sketch_text.stroke-79"),sQuery(id+"F9.wireOp",EDGE,"E12.sketch_text.stroke-80"),sQuery(id+"F9.wireOp",EDGE,"E12.sketch_text.stroke-81"),sQuery(id+"F9.wireOp",EDGE,"E12.sketch_text.stroke-82"),sQuery(id+"F9.wireOp",EDGE,"E12.sketch_text.stroke-83"),sQuery(id+"F9.wireOp",EDGE,"E12.sketch_text.stroke-84"),sQuery(id+"F9.wireOp",EDGE,"E12.sketch_text.stroke-85"),sQuery(id+"F9.wireOp",EDGE,"E12.sketch_text.stroke-86"),sQuery(id+"F9.wireOp",EDGE,"E12.sketch_text.stroke-87"),sQuery(id+"F9.wireOp",EDGE,"E12.sketch_text.stroke-88"),sQuery(id+"F9.wireOp",EDGE,"E12.sketch_text.stroke-89"),sQuery(id+"F9.wireOp",EDGE,"E12.sketch_text.stroke-90"),sQuery(id+"F9.wireOp",EDGE,"E12.sketch_text.stroke-91"),sQuery(id+"F9.wireOp",EDGE,"E12.sketch_text.stroke-92"),sQuery(id+"F9.wireOp",EDGE,"E12.sketch_text.stroke-93"),sQuery(id+"F9.wireOp",EDGE,"E12.sketch_text.stroke-94"),sQuery(id+"F9.wireOp",EDGE,"E12.sketch_text.stroke-95"),sQuery(id+"F9.wireOp",EDGE,"E12.sketch_text.stroke-96"),sQuery(id+"F9.wireOp",EDGE,"E12.sketch_text.stroke-97"),sQuery(id+"F9.wireOp",EDGE,"E12.sketch_text.stroke-98"),sQuery(id+"F9.wireOp",EDGE,"E12.sketch_text.stroke-99"),sQuery(id+"F9.wireOp",EDGE,"E12.sketch_text.stroke-100"),sQuery(id+"F9.wireOp",EDGE,"E12.sketch_text.stroke-101"),sQuery(id+"F9.wireOp",EDGE,"E12.sketch_text.stroke-102"),sQuery(id+"F9.wireOp",EDGE,"E12.sketch_text.stroke-103"),sQuery(id+"F9.wireOp",EDGE,"E12.sketch_text.stroke-104"),sQuery(id+"F9.wireOp",EDGE,"E12.sketch_text.stroke-105"),sQuery(id+"F9.wireOp",EDGE,"E12.sketch_text.stroke-106"),sQuery(id+"F9.wireOp",EDGE,"E12.sketch_text.stroke-107"),sQuery(id+"F9.wireOp",EDGE,"E12.sketch_text.stroke-108"),sQuery(id+"F9.wireOp",EDGE,"E12.sketch_text.stroke-109"),sQuery(id+"F9.wireOp",EDGE,"E12.sketch_text.stroke-110"),sQuery(id+"F9.wireOp",EDGE,"E12.sketch_text.stroke-111"),sQuery(id+"F9.wireOp",EDGE,"E12.sketch_text.stroke-112"),sQuery(id+"F9.wireOp",EDGE,"E12.sketch_text.stroke-113"),sQuery(id+"F9.wireOp",EDGE,"E12.sketch_text.stroke-114"),sQuery(id+"F9.wireOp",EDGE,"E12.sketch_text.stroke-115"),sQuery(id+"F9.wireOp",EDGE,"E12.sketch_text.stroke-116")])]});
            var Q21;
            Q21=makeQuery(id+"F11.opExtrude","SWEPT_BODY",BODY,{"disambiguationData":[OSD([sQuery(id+"F9.wireOp",EDGE,"E12.sketch_text.stroke-117"),sQuery(id+"F9.wireOp",EDGE,"E12.sketch_text.stroke-118"),sQuery(id+"F9.wireOp",EDGE,"E12.sketch_text.stroke-119"),sQuery(id+"F9.wireOp",EDGE,"E12.sketch_text.stroke-120"),sQuery(id+"F9.wireOp",EDGE,"E12.sketch_text.stroke-121"),sQuery(id+"F9.wireOp",EDGE,"E12.sketch_text.stroke-122"),sQuery(id+"F9.wireOp",EDGE,"E12.sketch_text.stroke-123"),sQuery(id+"F9.wireOp",EDGE,"E12.sketch_text.stroke-124"),sQuery(id+"F9.wireOp",EDGE,"E12.sketch_text.stroke-125"),sQuery(id+"F9.wireOp",EDGE,"E12.sketch_text.stroke-126"),sQuery(id+"F9.wireOp",EDGE,"E12.sketch_text.stroke-127"),sQuery(id+"F9.wireOp",EDGE,"E12.sketch_text.stroke-128"),sQuery(id+"F9.wireOp",EDGE,"E12.sketch_text.stroke-129"),sQuery(id+"F9.wireOp",EDGE,"E12.sketch_text.stroke-130"),sQuery(id+"F9.wireOp",EDGE,"E12.sketch_text.stroke-131"),sQuery(id+"F9.wireOp",EDGE,"E12.sketch_text.stroke-132"),sQuery(id+"F9.wireOp",EDGE,"E12.sketch_text.stroke-133"),sQuery(id+"F9.wireOp",EDGE,"E12.sketch_text.stroke-134"),sQuery(id+"F9.wireOp",EDGE,"E12.sketch_text.stroke-135")])]});
            var Q22;
            Q22=makeQuery(id+"F11.opExtrude","SWEPT_BODY",BODY,{"disambiguationData":[OSD([sQuery(id+"F9.wireOp",EDGE,"E12.sketch_text.stroke-136"),sQuery(id+"F9.wireOp",EDGE,"E12.sketch_text.stroke-137"),sQuery(id+"F9.wireOp",EDGE,"E12.sketch_text.stroke-138"),sQuery(id+"F9.wireOp",EDGE,"E12.sketch_text.stroke-139"),sQuery(id+"F9.wireOp",EDGE,"E12.sketch_text.stroke-140"),sQuery(id+"F9.wireOp",EDGE,"E12.sketch_text.stroke-141"),sQuery(id+"F9.wireOp",EDGE,"E12.sketch_text.stroke-142")])]});
            var Q23;
            Q23=makeQuery(id+"F11.opExtrude","SWEPT_BODY",BODY,{"disambiguationData":[OSD([sQuery(id+"F9.wireOp",EDGE,"E12.sketch_text.stroke-143"),sQuery(id+"F9.wireOp",EDGE,"E12.sketch_text.stroke-144"),sQuery(id+"F9.wireOp",EDGE,"E12.sketch_text.stroke-145"),sQuery(id+"F9.wireOp",EDGE,"E12.sketch_text.stroke-146"),sQuery(id+"F9.wireOp",EDGE,"E12.sketch_text.stroke-147"),sQuery(id+"F9.wireOp",EDGE,"E12.sketch_text.stroke-148"),sQuery(id+"F9.wireOp",EDGE,"E12.sketch_text.stroke-149"),sQuery(id+"F9.wireOp",EDGE,"E12.sketch_text.stroke-150"),sQuery(id+"F9.wireOp",EDGE,"E12.sketch_text.stroke-151"),sQuery(id+"F9.wireOp",EDGE,"E12.sketch_text.stroke-152"),sQuery(id+"F9.wireOp",EDGE,"E12.sketch_text.stroke-153"),sQuery(id+"F9.wireOp",EDGE,"E12.sketch_text.stroke-154"),sQuery(id+"F9.wireOp",EDGE,"E12.sketch_text.stroke-155"),sQuery(id+"F9.wireOp",EDGE,"E12.sketch_text.stroke-156"),sQuery(id+"F9.wireOp",EDGE,"E12.sketch_text.stroke-157"),sQuery(id+"F9.wireOp",EDGE,"E12.sketch_text.stroke-158"),sQuery(id+"F9.wireOp",EDGE,"E12.sketch_text.stroke-159"),sQuery(id+"F9.wireOp",EDGE,"E12.sketch_text.stroke-160"),sQuery(id+"F9.wireOp",EDGE,"E12.sketch_text.stroke-161"),sQuery(id+"F9.wireOp",EDGE,"E12.sketch_text.stroke-162"),sQuery(id+"F9.wireOp",EDGE,"E12.sketch_text.stroke-163"),sQuery(id+"F9.wireOp",EDGE,"E12.sketch_text.stroke-164"),sQuery(id+"F9.wireOp",EDGE,"E12.sketch_text.stroke-165"),sQuery(id+"F9.wireOp",EDGE,"E12.sketch_text.stroke-166"),sQuery(id+"F9.wireOp",EDGE,"E12.sketch_text.stroke-167"),sQuery(id+"F9.wireOp",EDGE,"E12.sketch_text.stroke-168"),sQuery(id+"F9.wireOp",EDGE,"E12.sketch_text.stroke-169"),sQuery(id+"F9.wireOp",EDGE,"E12.sketch_text.stroke-170")])]});
            var Q24;
            Q24=makeQuery(id+"F11.opExtrude","SWEPT_BODY",BODY,{"disambiguationData":[OSD([sQuery(id+"F9.wireOp",EDGE,"E12.sketch_text.stroke-171"),sQuery(id+"F9.wireOp",EDGE,"E12.sketch_text.stroke-172"),sQuery(id+"F9.wireOp",EDGE,"E12.sketch_text.stroke-173"),sQuery(id+"F9.wireOp",EDGE,"E12.sketch_text.stroke-174"),sQuery(id+"F9.wireOp",EDGE,"E12.sketch_text.stroke-175"),sQuery(id+"F9.wireOp",EDGE,"E12.sketch_text.stroke-176"),sQuery(id+"F9.wireOp",EDGE,"E12.sketch_text.stroke-177"),sQuery(id+"F9.wireOp",EDGE,"E12.sketch_text.stroke-178"),sQuery(id+"F9.wireOp",EDGE,"E12.sketch_text.stroke-179"),sQuery(id+"F9.wireOp",EDGE,"E12.sketch_text.stroke-180"),sQuery(id+"F9.wireOp",EDGE,"E12.sketch_text.stroke-181"),sQuery(id+"F9.wireOp",EDGE,"E12.sketch_text.stroke-182"),sQuery(id+"F9.wireOp",EDGE,"E12.sketch_text.stroke-183"),sQuery(id+"F9.wireOp",EDGE,"E12.sketch_text.stroke-184"),sQuery(id+"F9.wireOp",EDGE,"E12.sketch_text.stroke-185"),sQuery(id+"F9.wireOp",EDGE,"E12.sketch_text.stroke-186"),sQuery(id+"F9.wireOp",EDGE,"E12.sketch_text.stroke-187"),sQuery(id+"F9.wireOp",EDGE,"E12.sketch_text.stroke-188"),sQuery(id+"F9.wireOp",EDGE,"E12.sketch_text.stroke-189"),sQuery(id+"F9.wireOp",EDGE,"E12.sketch_text.stroke-190"),sQuery(id+"F9.wireOp",EDGE,"E12.sketch_text.stroke-191"),sQuery(id+"F9.wireOp",EDGE,"E12.sketch_text.stroke-192"),sQuery(id+"F9.wireOp",EDGE,"E12.sketch_text.stroke-193"),sQuery(id+"F9.wireOp",EDGE,"E12.sketch_text.stroke-194"),sQuery(id+"F9.wireOp",EDGE,"E12.sketch_text.stroke-195"),sQuery(id+"F9.wireOp",EDGE,"E12.sketch_text.stroke-196"),sQuery(id+"F9.wireOp",EDGE,"E12.sketch_text.stroke-197"),sQuery(id+"F9.wireOp",EDGE,"E12.sketch_text.stroke-198")])]});
            var Q25;
            Q25=makeQuery(id+"F11.opExtrude","SWEPT_BODY",BODY,{"disambiguationData":[OSD([sQuery(id+"F9.wireOp",EDGE,"E13.sketch_text.stroke-0"),sQuery(id+"F9.wireOp",EDGE,"E13.sketch_text.stroke-1"),sQuery(id+"F9.wireOp",EDGE,"E13.sketch_text.stroke-2"),sQuery(id+"F9.wireOp",EDGE,"E13.sketch_text.stroke-3"),sQuery(id+"F9.wireOp",EDGE,"E13.sketch_text.stroke-4"),sQuery(id+"F9.wireOp",EDGE,"E13.sketch_text.stroke-5"),sQuery(id+"F9.wireOp",EDGE,"E13.sketch_text.stroke-6"),sQuery(id+"F9.wireOp",EDGE,"E13.sketch_text.stroke-7"),sQuery(id+"F9.wireOp",EDGE,"E13.sketch_text.stroke-8")])]});
            var Q26;
            Q26=makeQuery(id+"F11.opExtrude","SWEPT_BODY",BODY,{"disambiguationData":[OSD([sQuery(id+"F9.wireOp",EDGE,"E13.sketch_text.stroke-9"),sQuery(id+"F9.wireOp",EDGE,"E13.sketch_text.stroke-10"),sQuery(id+"F9.wireOp",EDGE,"E13.sketch_text.stroke-11"),sQuery(id+"F9.wireOp",EDGE,"E13.sketch_text.stroke-12"),sQuery(id+"F9.wireOp",EDGE,"E13.sketch_text.stroke-13"),sQuery(id+"F9.wireOp",EDGE,"E13.sketch_text.stroke-14"),sQuery(id+"F9.wireOp",EDGE,"E13.sketch_text.stroke-15"),sQuery(id+"F9.wireOp",EDGE,"E13.sketch_text.stroke-16"),sQuery(id+"F9.wireOp",EDGE,"E13.sketch_text.stroke-17"),sQuery(id+"F9.wireOp",EDGE,"E13.sketch_text.stroke-18"),sQuery(id+"F9.wireOp",EDGE,"E13.sketch_text.stroke-19"),sQuery(id+"F9.wireOp",EDGE,"E13.sketch_text.stroke-20"),sQuery(id+"F9.wireOp",EDGE,"E13.sketch_text.stroke-21"),sQuery(id+"F9.wireOp",EDGE,"E13.sketch_text.stroke-22"),sQuery(id+"F9.wireOp",EDGE,"E13.sketch_text.stroke-23"),sQuery(id+"F9.wireOp",EDGE,"E13.sketch_text.stroke-24"),sQuery(id+"F9.wireOp",EDGE,"E13.sketch_text.stroke-25"),sQuery(id+"F9.wireOp",EDGE,"E13.sketch_text.stroke-26"),sQuery(id+"F9.wireOp",EDGE,"E13.sketch_text.stroke-27")])]});
            var Q27;
            Q27=makeQuery(id+"F11.opExtrude","SWEPT_BODY",BODY,{"disambiguationData":[OSD([sQuery(id+"F9.wireOp",EDGE,"E13.sketch_text.stroke-28"),sQuery(id+"F9.wireOp",EDGE,"E13.sketch_text.stroke-29"),sQuery(id+"F9.wireOp",EDGE,"E13.sketch_text.stroke-30"),sQuery(id+"F9.wireOp",EDGE,"E13.sketch_text.stroke-31")])]});
            var Q28;
            Q28=makeQuery(id+"F11.opExtrude","SWEPT_BODY",BODY,{"disambiguationData":[OSD([sQuery(id+"F9.wireOp",EDGE,"E13.sketch_text.stroke-32"),sQuery(id+"F9.wireOp",EDGE,"E13.sketch_text.stroke-33"),sQuery(id+"F9.wireOp",EDGE,"E13.sketch_text.stroke-34"),sQuery(id+"F9.wireOp",EDGE,"E13.sketch_text.stroke-35")])]});
            var Q29;
            Q29=makeQuery(id+"F11.opExtrude","SWEPT_BODY",BODY,{"disambiguationData":[OSD([sQuery(id+"F9.wireOp",EDGE,"E13.sketch_text.stroke-36"),sQuery(id+"F9.wireOp",EDGE,"E13.sketch_text.stroke-37"),sQuery(id+"F9.wireOp",EDGE,"E13.sketch_text.stroke-38"),sQuery(id+"F9.wireOp",EDGE,"E13.sketch_text.stroke-39"),sQuery(id+"F9.wireOp",EDGE,"E13.sketch_text.stroke-40"),sQuery(id+"F9.wireOp",EDGE,"E13.sketch_text.stroke-41"),sQuery(id+"F9.wireOp",EDGE,"E13.sketch_text.stroke-42"),sQuery(id+"F9.wireOp",EDGE,"E13.sketch_text.stroke-43"),sQuery(id+"F9.wireOp",EDGE,"E13.sketch_text.stroke-44"),sQuery(id+"F9.wireOp",EDGE,"E13.sketch_text.stroke-45"),sQuery(id+"F9.wireOp",EDGE,"E13.sketch_text.stroke-46"),sQuery(id+"F9.wireOp",EDGE,"E13.sketch_text.stroke-47"),sQuery(id+"F9.wireOp",EDGE,"E13.sketch_text.stroke-48"),sQuery(id+"F9.wireOp",EDGE,"E13.sketch_text.stroke-49"),sQuery(id+"F9.wireOp",EDGE,"E13.sketch_text.stroke-50"),sQuery(id+"F9.wireOp",EDGE,"E13.sketch_text.stroke-51"),sQuery(id+"F9.wireOp",EDGE,"E13.sketch_text.stroke-52")])]});
            var Q30;
            Q30=makeQuery(id+"F11.opExtrude","SWEPT_BODY",BODY,{"disambiguationData":[OSD([sQuery(id+"F9.wireOp",EDGE,"E13.sketch_text.stroke-53"),sQuery(id+"F9.wireOp",EDGE,"E13.sketch_text.stroke-54"),sQuery(id+"F9.wireOp",EDGE,"E13.sketch_text.stroke-55"),sQuery(id+"F9.wireOp",EDGE,"E13.sketch_text.stroke-56"),sQuery(id+"F9.wireOp",EDGE,"E13.sketch_text.stroke-57"),sQuery(id+"F9.wireOp",EDGE,"E13.sketch_text.stroke-58"),sQuery(id+"F9.wireOp",EDGE,"E13.sketch_text.stroke-59"),sQuery(id+"F9.wireOp",EDGE,"E13.sketch_text.stroke-60"),sQuery(id+"F9.wireOp",EDGE,"E13.sketch_text.stroke-61"),sQuery(id+"F9.wireOp",EDGE,"E13.sketch_text.stroke-62"),sQuery(id+"F9.wireOp",EDGE,"E13.sketch_text.stroke-63"),sQuery(id+"F9.wireOp",EDGE,"E13.sketch_text.stroke-64"),sQuery(id+"F9.wireOp",EDGE,"E13.sketch_text.stroke-65"),sQuery(id+"F9.wireOp",EDGE,"E13.sketch_text.stroke-66"),sQuery(id+"F9.wireOp",EDGE,"E13.sketch_text.stroke-67"),sQuery(id+"F9.wireOp",EDGE,"E13.sketch_text.stroke-68"),sQuery(id+"F9.wireOp",EDGE,"E13.sketch_text.stroke-69"),sQuery(id+"F9.wireOp",EDGE,"E13.sketch_text.stroke-70"),sQuery(id+"F9.wireOp",EDGE,"E13.sketch_text.stroke-71"),sQuery(id+"F9.wireOp",EDGE,"E13.sketch_text.stroke-72"),sQuery(id+"F9.wireOp",EDGE,"E13.sketch_text.stroke-73"),sQuery(id+"F9.wireOp",EDGE,"E13.sketch_text.stroke-74"),sQuery(id+"F9.wireOp",EDGE,"E13.sketch_text.stroke-75")])]});
            var Q31;
            Q31=makeQuery(id+"F11.opExtrude","SWEPT_BODY",BODY,{"disambiguationData":[OSD([sQuery(id+"F9.wireOp",EDGE,"E13.sketch_text.stroke-76"),sQuery(id+"F9.wireOp",EDGE,"E13.sketch_text.stroke-77"),sQuery(id+"F9.wireOp",EDGE,"E13.sketch_text.stroke-78"),sQuery(id+"F9.wireOp",EDGE,"E13.sketch_text.stroke-79"),sQuery(id+"F9.wireOp",EDGE,"E13.sketch_text.stroke-80"),sQuery(id+"F9.wireOp",EDGE,"E13.sketch_text.stroke-81"),sQuery(id+"F9.wireOp",EDGE,"E13.sketch_text.stroke-82"),sQuery(id+"F9.wireOp",EDGE,"E13.sketch_text.stroke-83"),sQuery(id+"F9.wireOp",EDGE,"E13.sketch_text.stroke-84"),sQuery(id+"F9.wireOp",EDGE,"E13.sketch_text.stroke-85"),sQuery(id+"F9.wireOp",EDGE,"E13.sketch_text.stroke-86"),sQuery(id+"F9.wireOp",EDGE,"E13.sketch_text.stroke-87"),sQuery(id+"F9.wireOp",EDGE,"E13.sketch_text.stroke-88"),sQuery(id+"F9.wireOp",EDGE,"E13.sketch_text.stroke-89"),sQuery(id+"F9.wireOp",EDGE,"E13.sketch_text.stroke-90"),sQuery(id+"F9.wireOp",EDGE,"E13.sketch_text.stroke-91"),sQuery(id+"F9.wireOp",EDGE,"E13.sketch_text.stroke-92"),sQuery(id+"F9.wireOp",EDGE,"E13.sketch_text.stroke-93"),sQuery(id+"F9.wireOp",EDGE,"E13.sketch_text.stroke-94"),sQuery(id+"F9.wireOp",EDGE,"E13.sketch_text.stroke-95"),sQuery(id+"F9.wireOp",EDGE,"E13.sketch_text.stroke-96"),sQuery(id+"F9.wireOp",EDGE,"E13.sketch_text.stroke-97"),sQuery(id+"F9.wireOp",EDGE,"E13.sketch_text.stroke-98"),sQuery(id+"F9.wireOp",EDGE,"E13.sketch_text.stroke-99"),sQuery(id+"F9.wireOp",EDGE,"E13.sketch_text.stroke-100"),sQuery(id+"F9.wireOp",EDGE,"E13.sketch_text.stroke-101"),sQuery(id+"F9.wireOp",EDGE,"E13.sketch_text.stroke-102"),sQuery(id+"F9.wireOp",EDGE,"E13.sketch_text.stroke-103"),sQuery(id+"F9.wireOp",EDGE,"E13.sketch_text.stroke-104"),sQuery(id+"F9.wireOp",EDGE,"E13.sketch_text.stroke-105"),sQuery(id+"F9.wireOp",EDGE,"E13.sketch_text.stroke-106")])]});
            var Q32;
            Q32=makeQuery(id+"F11.opExtrude","SWEPT_BODY",BODY,{"disambiguationData":[OSD([sQuery(id+"F9.wireOp",EDGE,"E13.sketch_text.stroke-107"),sQuery(id+"F9.wireOp",EDGE,"E13.sketch_text.stroke-108"),sQuery(id+"F9.wireOp",EDGE,"E13.sketch_text.stroke-109"),sQuery(id+"F9.wireOp",EDGE,"E13.sketch_text.stroke-110"),sQuery(id+"F9.wireOp",EDGE,"E13.sketch_text.stroke-111"),sQuery(id+"F9.wireOp",EDGE,"E13.sketch_text.stroke-112"),sQuery(id+"F9.wireOp",EDGE,"E13.sketch_text.stroke-113"),sQuery(id+"F9.wireOp",EDGE,"E13.sketch_text.stroke-114"),sQuery(id+"F9.wireOp",EDGE,"E13.sketch_text.stroke-115"),sQuery(id+"F9.wireOp",EDGE,"E13.sketch_text.stroke-116"),sQuery(id+"F9.wireOp",EDGE,"E13.sketch_text.stroke-117"),sQuery(id+"F9.wireOp",EDGE,"E13.sketch_text.stroke-118"),sQuery(id+"F9.wireOp",EDGE,"E13.sketch_text.stroke-119"),sQuery(id+"F9.wireOp",EDGE,"E13.sketch_text.stroke-120"),sQuery(id+"F9.wireOp",EDGE,"E13.sketch_text.stroke-121"),sQuery(id+"F9.wireOp",EDGE,"E13.sketch_text.stroke-122"),sQuery(id+"F9.wireOp",EDGE,"E13.sketch_text.stroke-123"),sQuery(id+"F9.wireOp",EDGE,"E13.sketch_text.stroke-124"),sQuery(id+"F9.wireOp",EDGE,"E13.sketch_text.stroke-125"),sQuery(id+"F9.wireOp",EDGE,"E13.sketch_text.stroke-126"),sQuery(id+"F9.wireOp",EDGE,"E13.sketch_text.stroke-127"),sQuery(id+"F9.wireOp",EDGE,"E13.sketch_text.stroke-128"),sQuery(id+"F9.wireOp",EDGE,"E13.sketch_text.stroke-129"),sQuery(id+"F9.wireOp",EDGE,"E13.sketch_text.stroke-130"),sQuery(id+"F9.wireOp",EDGE,"E13.sketch_text.stroke-131"),sQuery(id+"F9.wireOp",EDGE,"E13.sketch_text.stroke-132"),sQuery(id+"F9.wireOp",EDGE,"E13.sketch_text.stroke-133"),sQuery(id+"F9.wireOp",EDGE,"E13.sketch_text.stroke-134")])]});
            var Q33;
            Q33=makeQuery(id+"F11.opExtrude","SWEPT_BODY",BODY,{"disambiguationData":[OSD([sQuery(id+"F9.wireOp",EDGE,"E13.sketch_text.stroke-135"),sQuery(id+"F9.wireOp",EDGE,"E13.sketch_text.stroke-136"),sQuery(id+"F9.wireOp",EDGE,"E13.sketch_text.stroke-137"),sQuery(id+"F9.wireOp",EDGE,"E13.sketch_text.stroke-138"),sQuery(id+"F9.wireOp",EDGE,"E13.sketch_text.stroke-139"),sQuery(id+"F9.wireOp",EDGE,"E13.sketch_text.stroke-140"),sQuery(id+"F9.wireOp",EDGE,"E13.sketch_text.stroke-141"),sQuery(id+"F9.wireOp",EDGE,"E13.sketch_text.stroke-142"),sQuery(id+"F9.wireOp",EDGE,"E13.sketch_text.stroke-143"),sQuery(id+"F9.wireOp",EDGE,"E13.sketch_text.stroke-144"),sQuery(id+"F9.wireOp",EDGE,"E13.sketch_text.stroke-145"),sQuery(id+"F9.wireOp",EDGE,"E13.sketch_text.stroke-146"),sQuery(id+"F9.wireOp",EDGE,"E13.sketch_text.stroke-147"),sQuery(id+"F9.wireOp",EDGE,"E13.sketch_text.stroke-148"),sQuery(id+"F9.wireOp",EDGE,"E13.sketch_text.stroke-149"),sQuery(id+"F9.wireOp",EDGE,"E13.sketch_text.stroke-150"),sQuery(id+"F9.wireOp",EDGE,"E13.sketch_text.stroke-151"),sQuery(id+"F9.wireOp",EDGE,"E13.sketch_text.stroke-152"),sQuery(id+"F9.wireOp",EDGE,"E13.sketch_text.stroke-153"),sQuery(id+"F9.wireOp",EDGE,"E13.sketch_text.stroke-154"),sQuery(id+"F9.wireOp",EDGE,"E13.sketch_text.stroke-155"),sQuery(id+"F9.wireOp",EDGE,"E13.sketch_text.stroke-156"),sQuery(id+"F9.wireOp",EDGE,"E13.sketch_text.stroke-157"),sQuery(id+"F9.wireOp",EDGE,"E13.sketch_text.stroke-158"),sQuery(id+"F9.wireOp",EDGE,"E13.sketch_text.stroke-159"),sQuery(id+"F9.wireOp",EDGE,"E13.sketch_text.stroke-160"),sQuery(id+"F9.wireOp",EDGE,"E13.sketch_text.stroke-161"),sQuery(id+"F9.wireOp",EDGE,"E13.sketch_text.stroke-162")])]});
            var Q34;
            Q34=makeQuery(id+"F14.opExtrude","SWEPT_BODY",BODY,{"disambiguationData":[OSD([sQuery(id+"F13.wireOp",EDGE,"E24.bottom"),sQuery(id+"F13.wireOp",EDGE,"E24.top"),sQuery(id+"F13.wireOp",EDGE,"E24.left"),sQuery(id+"F13.wireOp",EDGE,"E24.right")])]});
            var Q35;
            Q35=makeQuery(id+"F14.opExtrude","SWEPT_BODY",BODY,{"disambiguationData":[OSD([sQuery(id+"F13.wireOp",EDGE,"E25.bottom"),sQuery(id+"F13.wireOp",EDGE,"E25.top"),sQuery(id+"F13.wireOp",EDGE,"E25.left"),sQuery(id+"F13.wireOp",EDGE,"E25.right")])]});
            booleanBodies(context, id + "F19", {"operationType" : BooleanOperationType.UNION, "tools" : qUnion([Q0, Q1, Q2, Q3, Q4, Q5, Q6, Q7, Q8, Q9, Q10, Q11, Q12, Q13, Q14, Q15, Q16, Q17, Q18, Q19, Q20, Q21, Q22, Q23, Q24, Q25, Q26, Q27, Q28, Q29, Q30, Q31, Q32, Q33, Q34, Q35])});
        }
        {
            var Q0;
            Q0=makeQuery(id+"F10.boolean.opBoolean","INTERSECT",EDGE,{"derivedFrom":[makeQuery(id+"F1.opExtrude","SWEPT_FACE",FACE,{"disambiguationData":[OSD([sQuery(id+"F0.wireOp",EDGE,"E4")])]}),makeQuery(id+"F10.opExtrude","SWEPT_FACE",FACE,{"disambiguationData":[OSD([sQuery(id+"F9.wireOp",EDGE,"E14.right")])]})]});
            var Q1;
            Q1=makeQuery(id+"F10.boolean.opBoolean","INTERSECT",EDGE,{"derivedFrom":[makeQuery(id+"F1.opExtrude","SWEPT_FACE",FACE,{"disambiguationData":[OSD([sQuery(id+"F0.wireOp",EDGE,"E5.1.0.0")])]}),makeQuery(id+"F10.opExtrude","SWEPT_FACE",FACE,{"disambiguationData":[OSD([sQuery(id+"F9.wireOp",EDGE,"E15.right")])]})]});
            var Q2;
            Q2=makeQuery(id+"F10.boolean.opBoolean","INTERSECT",EDGE,{"derivedFrom":[makeQuery(id+"F1.opExtrude","SWEPT_FACE",FACE,{"disambiguationData":[OSD([sQuery(id+"F0.wireOp",EDGE,"E5.2.0.0")])]}),makeQuery(id+"F10.opExtrude","SWEPT_FACE",FACE,{"disambiguationData":[OSD([sQuery(id+"F9.wireOp",EDGE,"E16.right")])]})]});
            var Q3;
            Q3=makeQuery(id+"F19.opBoolean","INTERSECT",EDGE,{"derivedFrom":[makeQuery(id+"F1.opExtrude","SWEPT_FACE",FACE,{"disambiguationData":[OSD([sQuery(id+"F0.wireOp",EDGE,"E7.2.0.0")])]}),makeQuery(id+"F14.opExtrude","SWEPT_FACE",FACE,{"disambiguationData":[OSD([sQuery(id+"F13.wireOp",EDGE,"E24.left")])]})]});
            var Q4;
            Q4=makeQuery(id+"F19.opBoolean","INTERSECT",EDGE,{"derivedFrom":[makeQuery(id+"F1.opExtrude","SWEPT_FACE",FACE,{"disambiguationData":[OSD([sQuery(id+"F0.wireOp",EDGE,"E7.1.0.0")])]}),makeQuery(id+"F14.opExtrude","SWEPT_FACE",FACE,{"disambiguationData":[OSD([sQuery(id+"F13.wireOp",EDGE,"E25.left")])]})]});
            var Q5;
            Q5=makeQuery(id+"F19.opBoolean","INTERSECT",EDGE,{"derivedFrom":[makeQuery(id+"F1.opExtrude","SWEPT_FACE",FACE,{"disambiguationData":[OSD([sQuery(id+"F0.wireOp",EDGE,"E6")])]}),makeQuery(id+"F14.opExtrude","SWEPT_FACE",FACE,{"disambiguationData":[OSD([sQuery(id+"F13.wireOp",EDGE,"E26.left")])]})]});
            fillet(context, id + "F20", {"entities" : qUnion([Q0, Q1, Q2, Q3, Q4, Q5]), "radius" : 1 * mm, "tangentPropagation" : true, "allowEdgeOverflow" : false});
        }
    });
